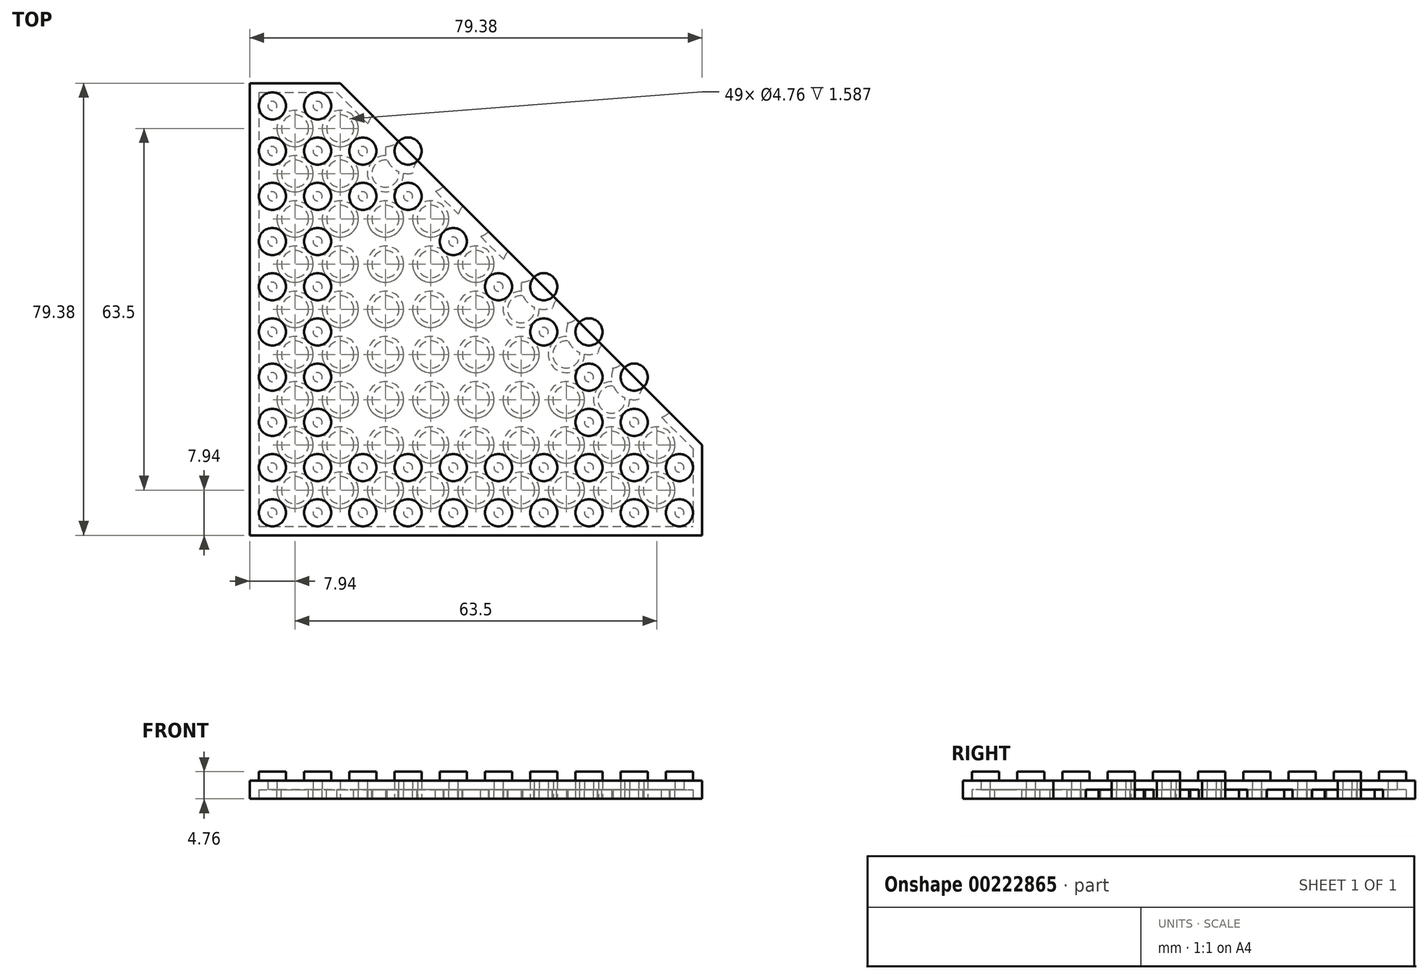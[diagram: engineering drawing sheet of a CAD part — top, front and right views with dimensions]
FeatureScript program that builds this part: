
annotation { "Feature Type Name" : "Feature", "Feature Type Description" : "" }
export const myFeature = defineFeature(function(context is Context, id is Id, definition is map)
    precondition{}
    {
        {
            var Q0;
            Q0=qCreatedBy(makeId("Top.planeOp"),FACE);
            var sketch = newSketch(context, id + "F0", { "sketchPlane" : qUnion([Q0])});
            skLineSegment(sketch, "E0.bottom", {"start": v(-39.69, 39.69) * mm, "end": v(39.69, 39.69) * mm});
            skLineSegment(sketch, "E0.top", {"start": v(-39.69, -39.69) * mm, "end": v(39.69, -39.69) * mm});
            skLineSegment(sketch, "E0.left", {"start": v(-39.69, 39.69) * mm, "end": v(-39.69, -39.69) * mm});
            skLineSegment(sketch, "E0.right", {"start": v(39.69, 39.69) * mm, "end": v(39.69, -39.69) * mm});
            skPoint(sketch, "E0.middle", {"position": v(0, 0) * mm});
            skCircle(sketch, "E1", {"center": v(-35.72, -35.72) * mm, "radius": 2.38 * mm});
            skCircle(sketch, "E2.0.1.0", {"center": v(-35.72, -27.78) * mm, "radius": 2.38 * mm});
            skCircle(sketch, "E2.0.2.0", {"center": v(-35.72, -19.84) * mm, "radius": 2.38 * mm});
            skCircle(sketch, "E2.0.3.0", {"center": v(-35.72, -11.9) * mm, "radius": 2.38 * mm});
            skCircle(sketch, "E2.0.4.0", {"center": v(-35.72, -3.97) * mm, "radius": 2.38 * mm});
            skCircle(sketch, "E2.0.5.0", {"center": v(-35.72, 3.97) * mm, "radius": 2.38 * mm});
            skCircle(sketch, "E2.0.6.0", {"center": v(-35.72, 11.9) * mm, "radius": 2.38 * mm});
            skCircle(sketch, "E2.0.7.0", {"center": v(-35.72, 19.84) * mm, "radius": 2.38 * mm});
            skCircle(sketch, "E2.0.8.0", {"center": v(-35.72, 27.78) * mm, "radius": 2.38 * mm});
            skCircle(sketch, "E2.0.9.0", {"center": v(-35.72, 35.72) * mm, "radius": 2.38 * mm});
            skCircle(sketch, "E2.1.0.0", {"center": v(-27.78, -35.72) * mm, "radius": 2.38 * mm});
            skCircle(sketch, "E2.1.1.0", {"center": v(-27.78, -27.78) * mm, "radius": 2.38 * mm});
            skCircle(sketch, "E2.1.2.0", {"center": v(-27.78, -19.84) * mm, "radius": 2.38 * mm});
            skCircle(sketch, "E2.1.3.0", {"center": v(-27.78, -11.9) * mm, "radius": 2.38 * mm});
            skCircle(sketch, "E2.1.4.0", {"center": v(-27.78, -3.97) * mm, "radius": 2.38 * mm});
            skCircle(sketch, "E2.1.5.0", {"center": v(-27.78, 3.97) * mm, "radius": 2.38 * mm});
            skCircle(sketch, "E2.1.6.0", {"center": v(-27.78, 11.9) * mm, "radius": 2.38 * mm});
            skCircle(sketch, "E2.1.7.0", {"center": v(-27.78, 19.84) * mm, "radius": 2.38 * mm});
            skCircle(sketch, "E2.1.8.0", {"center": v(-27.78, 27.78) * mm, "radius": 2.38 * mm});
            skCircle(sketch, "E2.1.9.0", {"center": v(-27.78, 35.72) * mm, "radius": 2.38 * mm});
            skCircle(sketch, "E2.2.0.0", {"center": v(-19.84, -35.72) * mm, "radius": 2.38 * mm});
            skCircle(sketch, "E2.2.1.0", {"center": v(-19.84, -27.78) * mm, "radius": 2.38 * mm});
            skCircle(sketch, "E2.2.2.0", {"center": v(-19.84, -19.84) * mm, "radius": 2.38 * mm});
            skCircle(sketch, "E2.2.3.0", {"center": v(-19.84, -11.9) * mm, "radius": 2.38 * mm});
            skCircle(sketch, "E2.2.4.0", {"center": v(-19.84, -3.97) * mm, "radius": 2.38 * mm});
            skCircle(sketch, "E2.2.5.0", {"center": v(-19.84, 3.97) * mm, "radius": 2.38 * mm});
            skCircle(sketch, "E2.2.6.0", {"center": v(-19.84, 11.9) * mm, "radius": 2.38 * mm});
            skCircle(sketch, "E2.2.7.0", {"center": v(-19.84, 19.84) * mm, "radius": 2.38 * mm});
            skCircle(sketch, "E2.2.8.0", {"center": v(-19.84, 27.78) * mm, "radius": 2.38 * mm});
            skCircle(sketch, "E2.2.9.0", {"center": v(-19.84, 35.72) * mm, "radius": 2.38 * mm});
            skCircle(sketch, "E2.3.0.0", {"center": v(-11.9, -35.72) * mm, "radius": 2.38 * mm});
            skCircle(sketch, "E2.3.1.0", {"center": v(-11.9, -27.78) * mm, "radius": 2.38 * mm});
            skCircle(sketch, "E2.3.2.0", {"center": v(-11.9, -19.84) * mm, "radius": 2.38 * mm});
            skCircle(sketch, "E2.3.3.0", {"center": v(-11.9, -11.9) * mm, "radius": 2.38 * mm});
            skCircle(sketch, "E2.3.4.0", {"center": v(-11.9, -3.97) * mm, "radius": 2.38 * mm});
            skCircle(sketch, "E2.3.5.0", {"center": v(-11.9, 3.97) * mm, "radius": 2.38 * mm});
            skCircle(sketch, "E2.3.6.0", {"center": v(-11.9, 11.9) * mm, "radius": 2.38 * mm});
            skCircle(sketch, "E2.3.7.0", {"center": v(-11.9, 19.84) * mm, "radius": 2.38 * mm});
            skCircle(sketch, "E2.3.8.0", {"center": v(-11.9, 27.78) * mm, "radius": 2.38 * mm});
            skCircle(sketch, "E2.3.9.0", {"center": v(-11.9, 35.72) * mm, "radius": 2.38 * mm});
            skCircle(sketch, "E2.4.0.0", {"center": v(-3.97, -35.72) * mm, "radius": 2.38 * mm});
            skCircle(sketch, "E2.4.1.0", {"center": v(-3.97, -27.78) * mm, "radius": 2.38 * mm});
            skCircle(sketch, "E2.4.2.0", {"center": v(-3.97, -19.84) * mm, "radius": 2.38 * mm});
            skCircle(sketch, "E2.4.3.0", {"center": v(-3.97, -11.9) * mm, "radius": 2.38 * mm});
            skCircle(sketch, "E2.4.4.0", {"center": v(-3.97, -3.97) * mm, "radius": 2.38 * mm});
            skCircle(sketch, "E2.4.5.0", {"center": v(-3.97, 3.97) * mm, "radius": 2.38 * mm});
            skCircle(sketch, "E2.4.6.0", {"center": v(-3.97, 11.9) * mm, "radius": 2.38 * mm});
            skCircle(sketch, "E2.4.7.0", {"center": v(-3.97, 19.84) * mm, "radius": 2.38 * mm});
            skCircle(sketch, "E2.4.8.0", {"center": v(-3.97, 27.78) * mm, "radius": 2.38 * mm});
            skCircle(sketch, "E2.4.9.0", {"center": v(-3.97, 35.72) * mm, "radius": 2.38 * mm});
            skCircle(sketch, "E2.5.0.0", {"center": v(3.97, -35.72) * mm, "radius": 2.38 * mm});
            skCircle(sketch, "E2.5.1.0", {"center": v(3.97, -27.78) * mm, "radius": 2.38 * mm});
            skCircle(sketch, "E2.5.2.0", {"center": v(3.97, -19.84) * mm, "radius": 2.38 * mm});
            skCircle(sketch, "E2.5.3.0", {"center": v(3.97, -11.9) * mm, "radius": 2.38 * mm});
            skCircle(sketch, "E2.5.4.0", {"center": v(3.97, -3.97) * mm, "radius": 2.38 * mm});
            skCircle(sketch, "E2.5.5.0", {"center": v(3.97, 3.97) * mm, "radius": 2.38 * mm});
            skCircle(sketch, "E2.5.6.0", {"center": v(3.97, 11.9) * mm, "radius": 2.38 * mm});
            skCircle(sketch, "E2.5.7.0", {"center": v(3.97, 19.84) * mm, "radius": 2.38 * mm});
            skCircle(sketch, "E2.5.8.0", {"center": v(3.97, 27.78) * mm, "radius": 2.38 * mm});
            skCircle(sketch, "E2.5.9.0", {"center": v(3.97, 35.72) * mm, "radius": 2.38 * mm});
            skCircle(sketch, "E2.6.0.0", {"center": v(11.9, -35.72) * mm, "radius": 2.38 * mm});
            skCircle(sketch, "E2.6.1.0", {"center": v(11.9, -27.78) * mm, "radius": 2.38 * mm});
            skCircle(sketch, "E2.6.2.0", {"center": v(11.9, -19.84) * mm, "radius": 2.38 * mm});
            skCircle(sketch, "E2.6.3.0", {"center": v(11.9, -11.9) * mm, "radius": 2.38 * mm});
            skCircle(sketch, "E2.6.4.0", {"center": v(11.9, -3.97) * mm, "radius": 2.38 * mm});
            skCircle(sketch, "E2.6.5.0", {"center": v(11.9, 3.97) * mm, "radius": 2.38 * mm});
            skCircle(sketch, "E2.6.6.0", {"center": v(11.9, 11.9) * mm, "radius": 2.38 * mm});
            skCircle(sketch, "E2.6.7.0", {"center": v(11.9, 19.84) * mm, "radius": 2.38 * mm});
            skCircle(sketch, "E2.6.8.0", {"center": v(11.9, 27.78) * mm, "radius": 2.38 * mm});
            skCircle(sketch, "E2.6.9.0", {"center": v(11.9, 35.72) * mm, "radius": 2.38 * mm});
            skCircle(sketch, "E2.7.0.0", {"center": v(19.84, -35.72) * mm, "radius": 2.38 * mm});
            skCircle(sketch, "E2.7.1.0", {"center": v(19.84, -27.78) * mm, "radius": 2.38 * mm});
            skCircle(sketch, "E2.7.2.0", {"center": v(19.84, -19.84) * mm, "radius": 2.38 * mm});
            skCircle(sketch, "E2.7.3.0", {"center": v(19.84, -11.9) * mm, "radius": 2.38 * mm});
            skCircle(sketch, "E2.7.4.0", {"center": v(19.84, -3.97) * mm, "radius": 2.38 * mm});
            skCircle(sketch, "E2.7.5.0", {"center": v(19.84, 3.97) * mm, "radius": 2.38 * mm});
            skCircle(sketch, "E2.7.6.0", {"center": v(19.84, 11.9) * mm, "radius": 2.38 * mm});
            skCircle(sketch, "E2.7.7.0", {"center": v(19.84, 19.84) * mm, "radius": 2.38 * mm});
            skCircle(sketch, "E2.7.8.0", {"center": v(19.84, 27.78) * mm, "radius": 2.38 * mm});
            skCircle(sketch, "E2.7.9.0", {"center": v(19.84, 35.72) * mm, "radius": 2.38 * mm});
            skCircle(sketch, "E2.8.0.0", {"center": v(27.78, -35.72) * mm, "radius": 2.38 * mm});
            skCircle(sketch, "E2.8.1.0", {"center": v(27.78, -27.78) * mm, "radius": 2.38 * mm});
            skCircle(sketch, "E2.8.2.0", {"center": v(27.78, -19.84) * mm, "radius": 2.38 * mm});
            skCircle(sketch, "E2.8.3.0", {"center": v(27.78, -11.9) * mm, "radius": 2.38 * mm});
            skCircle(sketch, "E2.8.4.0", {"center": v(27.78, -3.97) * mm, "radius": 2.38 * mm});
            skCircle(sketch, "E2.8.5.0", {"center": v(27.78, 3.97) * mm, "radius": 2.38 * mm});
            skCircle(sketch, "E2.8.6.0", {"center": v(27.78, 11.9) * mm, "radius": 2.38 * mm});
            skCircle(sketch, "E2.8.7.0", {"center": v(27.78, 19.84) * mm, "radius": 2.38 * mm});
            skCircle(sketch, "E2.8.8.0", {"center": v(27.78, 27.78) * mm, "radius": 2.38 * mm});
            skCircle(sketch, "E2.8.9.0", {"center": v(27.78, 35.72) * mm, "radius": 2.38 * mm});
            skCircle(sketch, "E2.9.0.0", {"center": v(35.72, -35.72) * mm, "radius": 2.38 * mm});
            skCircle(sketch, "E2.9.1.0", {"center": v(35.72, -27.78) * mm, "radius": 2.38 * mm});
            skCircle(sketch, "E2.9.2.0", {"center": v(35.72, -19.84) * mm, "radius": 2.38 * mm});
            skCircle(sketch, "E2.9.3.0", {"center": v(35.72, -11.9) * mm, "radius": 2.38 * mm});
            skCircle(sketch, "E2.9.4.0", {"center": v(35.72, -3.97) * mm, "radius": 2.38 * mm});
            skCircle(sketch, "E2.9.5.0", {"center": v(35.72, 3.97) * mm, "radius": 2.38 * mm});
            skCircle(sketch, "E2.9.6.0", {"center": v(35.72, 11.9) * mm, "radius": 2.38 * mm});
            skCircle(sketch, "E2.9.7.0", {"center": v(35.72, 19.84) * mm, "radius": 2.38 * mm});
            skCircle(sketch, "E2.9.8.0", {"center": v(35.72, 27.78) * mm, "radius": 2.38 * mm});
            skCircle(sketch, "E2.9.9.0", {"center": v(35.72, 35.72) * mm, "radius": 2.38 * mm});
            skLineSegment(sketch, "E2.direction1", {"start": v(-35.72, -35.72) * mm, "end": v(-27.78, -35.72) * mm, "construction": true});
            skLineSegment(sketch, "E2.direction2", {"start": v(-35.72, -35.72) * mm, "end": v(-35.72, -27.78) * mm, "construction": true});
            skPoint(sketch, "E3", {"position": v(-23.81, 39.69) * mm});
            skPoint(sketch, "E4", {"position": v(39.69, -23.81) * mm});
            skLineSegment(sketch, "E5", {"start": v(-23.81, 39.69) * mm, "end": v(39.69, -23.81) * mm});
            skSolve(sketch);
        }
        {
            var Q0;
            {var subQ9=sQuery(id+"F0.wireOp",EDGE,"E0.top");Q0=makeQuery(id+"F0.imprint","IMPRINT",FACE,{"disambiguationData":[TD([[makeQuery(id+"F0.imprint","IMPRINT",EDGE,{"derivedFrom":subQ9}),1.0]])]});}
            var Q1;
            {var subQ0=sQuery(id+"F0.wireOp",EDGE,"E5");var subQ1=sQuery(id+"F0.wireOp",EDGE,"E2.2.9.0");var subQ2=makeQuery(id+"F0.imprint","INTERSECT",VERTEX,{"disambiguationData":[OD(0.0)],"derivedFrom":[subQ1,subQ0]});Q1=makeQuery(id+"F0.imprint","IMPRINT",FACE,{"disambiguationData":[TD([[makeQuery(id+"F0.imprint","IMPRINT",EDGE,{"disambiguationData":[TD([[subQ2,-1.0]])],"derivedFrom":subQ1}),1.0]])]});}
            var Q2;
            {var subQ0=sQuery(id+"F0.wireOp",EDGE,"E5");var subQ1=sQuery(id+"F0.wireOp",EDGE,"E2.3.8.0");var subQ2=makeQuery(id+"F0.imprint","INTERSECT",VERTEX,{"disambiguationData":[OD(0.0)],"derivedFrom":[subQ1,subQ0]});Q2=makeQuery(id+"F0.imprint","IMPRINT",FACE,{"disambiguationData":[TD([[makeQuery(id+"F0.imprint","IMPRINT",EDGE,{"disambiguationData":[TD([[subQ2,-1.0]])],"derivedFrom":subQ1}),1.0]])]});}
            var Q3;
            {var subQ0=sQuery(id+"F0.wireOp",EDGE,"E5");var subQ1=sQuery(id+"F0.wireOp",EDGE,"E2.4.7.0");var subQ2=makeQuery(id+"F0.imprint","INTERSECT",VERTEX,{"disambiguationData":[OD(0.0)],"derivedFrom":[subQ1,subQ0]});Q3=makeQuery(id+"F0.imprint","IMPRINT",FACE,{"disambiguationData":[TD([[makeQuery(id+"F0.imprint","IMPRINT",EDGE,{"disambiguationData":[TD([[subQ2,-1.0]])],"derivedFrom":subQ1}),1.0]])]});}
            var Q4;
            {var subQ0=sQuery(id+"F0.wireOp",EDGE,"E5");var subQ1=sQuery(id+"F0.wireOp",EDGE,"E2.5.6.0");var subQ2=makeQuery(id+"F0.imprint","INTERSECT",VERTEX,{"disambiguationData":[OD(0.0)],"derivedFrom":[subQ1,subQ0]});Q4=makeQuery(id+"F0.imprint","IMPRINT",FACE,{"disambiguationData":[TD([[makeQuery(id+"F0.imprint","IMPRINT",EDGE,{"disambiguationData":[TD([[subQ2,-1.0]])],"derivedFrom":subQ1}),1.0]])]});}
            var Q5;
            {var subQ0=sQuery(id+"F0.wireOp",EDGE,"E5");var subQ1=sQuery(id+"F0.wireOp",EDGE,"E2.6.5.0");var subQ2=makeQuery(id+"F0.imprint","INTERSECT",VERTEX,{"disambiguationData":[OD(0.0)],"derivedFrom":[subQ1,subQ0]});Q5=makeQuery(id+"F0.imprint","IMPRINT",FACE,{"disambiguationData":[TD([[makeQuery(id+"F0.imprint","IMPRINT",EDGE,{"disambiguationData":[TD([[subQ2,-1.0]])],"derivedFrom":subQ1}),1.0]])]});}
            var Q6;
            {var subQ0=sQuery(id+"F0.wireOp",EDGE,"E5");var subQ1=sQuery(id+"F0.wireOp",EDGE,"E2.7.4.0");var subQ2=makeQuery(id+"F0.imprint","INTERSECT",VERTEX,{"disambiguationData":[OD(0.0)],"derivedFrom":[subQ1,subQ0]});Q6=makeQuery(id+"F0.imprint","IMPRINT",FACE,{"disambiguationData":[TD([[makeQuery(id+"F0.imprint","IMPRINT",EDGE,{"disambiguationData":[TD([[subQ2,-1.0]])],"derivedFrom":subQ1}),1.0]])]});}
            var Q7;
            {var subQ0=sQuery(id+"F0.wireOp",EDGE,"E5");var subQ1=sQuery(id+"F0.wireOp",EDGE,"E2.8.3.0");var subQ2=makeQuery(id+"F0.imprint","INTERSECT",VERTEX,{"disambiguationData":[OD(0.0)],"derivedFrom":[subQ1,subQ0]});Q7=makeQuery(id+"F0.imprint","IMPRINT",FACE,{"disambiguationData":[TD([[makeQuery(id+"F0.imprint","IMPRINT",EDGE,{"disambiguationData":[TD([[subQ2,-1.0]])],"derivedFrom":subQ1}),1.0]])]});}
            var Q8;
            {var subQ0=sQuery(id+"F0.wireOp",EDGE,"E5");var subQ1=sQuery(id+"F0.wireOp",EDGE,"E2.9.2.0");var subQ2=makeQuery(id+"F0.imprint","INTERSECT",VERTEX,{"disambiguationData":[OD(0.0)],"derivedFrom":[subQ1,subQ0]});Q8=makeQuery(id+"F0.imprint","IMPRINT",FACE,{"disambiguationData":[TD([[makeQuery(id+"F0.imprint","IMPRINT",EDGE,{"disambiguationData":[TD([[subQ2,-1.0]])],"derivedFrom":subQ1}),1.0]])]});}
            var Q9;
            Q9=makeQuery(id+"F0.imprint","IMPRINT",FACE,{"disambiguationData":[TD([[makeQuery(id+"F0.imprint","IMPRINT",EDGE,{"derivedFrom":sQuery(id+"F0.wireOp",EDGE,"E2.2.6.0")}),1.0]])]});
            var Q10;
            Q10=makeQuery(id+"F0.imprint","IMPRINT",FACE,{"disambiguationData":[TD([[makeQuery(id+"F0.imprint","IMPRINT",EDGE,{"derivedFrom":sQuery(id+"F0.wireOp",EDGE,"E2.3.6.0")}),1.0]])]});
            var Q11;
            Q11=makeQuery(id+"F0.imprint","IMPRINT",FACE,{"disambiguationData":[TD([[makeQuery(id+"F0.imprint","IMPRINT",EDGE,{"derivedFrom":sQuery(id+"F0.wireOp",EDGE,"E2.2.5.0")}),1.0]])]});
            var Q12;
            Q12=makeQuery(id+"F0.imprint","IMPRINT",FACE,{"disambiguationData":[TD([[makeQuery(id+"F0.imprint","IMPRINT",EDGE,{"derivedFrom":sQuery(id+"F0.wireOp",EDGE,"E2.3.5.0")}),1.0]])]});
            var Q13;
            Q13=makeQuery(id+"F0.imprint","IMPRINT",FACE,{"disambiguationData":[TD([[makeQuery(id+"F0.imprint","IMPRINT",EDGE,{"derivedFrom":sQuery(id+"F0.wireOp",EDGE,"E2.2.4.0")}),1.0]])]});
            var Q14;
            Q14=makeQuery(id+"F0.imprint","IMPRINT",FACE,{"disambiguationData":[TD([[makeQuery(id+"F0.imprint","IMPRINT",EDGE,{"derivedFrom":sQuery(id+"F0.wireOp",EDGE,"E2.2.3.0")}),1.0]])]});
            var Q15;
            Q15=makeQuery(id+"F0.imprint","IMPRINT",FACE,{"disambiguationData":[TD([[makeQuery(id+"F0.imprint","IMPRINT",EDGE,{"derivedFrom":sQuery(id+"F0.wireOp",EDGE,"E2.2.2.0")}),1.0]])]});
            var Q16;
            Q16=makeQuery(id+"F0.imprint","IMPRINT",FACE,{"disambiguationData":[TD([[makeQuery(id+"F0.imprint","IMPRINT",EDGE,{"derivedFrom":sQuery(id+"F0.wireOp",EDGE,"E2.3.2.0")}),1.0]])]});
            var Q17;
            Q17=makeQuery(id+"F0.imprint","IMPRINT",FACE,{"disambiguationData":[TD([[makeQuery(id+"F0.imprint","IMPRINT",EDGE,{"derivedFrom":sQuery(id+"F0.wireOp",EDGE,"E2.4.2.0")}),1.0]])]});
            var Q18;
            Q18=makeQuery(id+"F0.imprint","IMPRINT",FACE,{"disambiguationData":[TD([[makeQuery(id+"F0.imprint","IMPRINT",EDGE,{"derivedFrom":sQuery(id+"F0.wireOp",EDGE,"E2.6.2.0")}),1.0]])]});
            var Q19;
            Q19=makeQuery(id+"F0.imprint","IMPRINT",FACE,{"disambiguationData":[TD([[makeQuery(id+"F0.imprint","IMPRINT",EDGE,{"derivedFrom":sQuery(id+"F0.wireOp",EDGE,"E2.6.3.0")}),1.0]])]});
            var Q20;
            Q20=makeQuery(id+"F0.imprint","IMPRINT",FACE,{"disambiguationData":[TD([[makeQuery(id+"F0.imprint","IMPRINT",EDGE,{"derivedFrom":sQuery(id+"F0.wireOp",EDGE,"E2.5.4.0")}),1.0]])]});
            var Q21;
            Q21=makeQuery(id+"F0.imprint","IMPRINT",FACE,{"disambiguationData":[TD([[makeQuery(id+"F0.imprint","IMPRINT",EDGE,{"derivedFrom":sQuery(id+"F0.wireOp",EDGE,"E2.4.5.0")}),1.0]])]});
            var Q22;
            Q22=makeQuery(id+"F0.imprint","IMPRINT",FACE,{"disambiguationData":[TD([[makeQuery(id+"F0.imprint","IMPRINT",EDGE,{"derivedFrom":sQuery(id+"F0.wireOp",EDGE,"E2.5.2.0")}),1.0]])]});
            var Q23;
            Q23=makeQuery(id+"F0.imprint","IMPRINT",FACE,{"disambiguationData":[TD([[makeQuery(id+"F0.imprint","IMPRINT",EDGE,{"derivedFrom":sQuery(id+"F0.wireOp",EDGE,"E2.5.3.0")}),1.0]])]});
            var Q24;
            Q24=makeQuery(id+"F0.imprint","IMPRINT",FACE,{"disambiguationData":[TD([[makeQuery(id+"F0.imprint","IMPRINT",EDGE,{"derivedFrom":sQuery(id+"F0.wireOp",EDGE,"E2.4.3.0")}),1.0]])]});
            var Q25;
            Q25=makeQuery(id+"F0.imprint","IMPRINT",FACE,{"disambiguationData":[TD([[makeQuery(id+"F0.imprint","IMPRINT",EDGE,{"derivedFrom":sQuery(id+"F0.wireOp",EDGE,"E2.3.3.0")}),1.0]])]});
            var Q26;
            Q26=makeQuery(id+"F0.imprint","IMPRINT",FACE,{"disambiguationData":[TD([[makeQuery(id+"F0.imprint","IMPRINT",EDGE,{"derivedFrom":sQuery(id+"F0.wireOp",EDGE,"E2.3.4.0")}),1.0]])]});
            var Q27;
            Q27=makeQuery(id+"F0.imprint","IMPRINT",FACE,{"disambiguationData":[TD([[makeQuery(id+"F0.imprint","IMPRINT",EDGE,{"derivedFrom":sQuery(id+"F0.wireOp",EDGE,"E2.4.4.0")}),1.0]])]});
            extrude(context, id + "F1", {"entities" : qUnion([Q0, Q1, Q2, Q3, Q4, Q5, Q6, Q7, Q8, Q9, Q10, Q11, Q12, Q13, Q14, Q15, Q16, Q17, Q18, Q19, Q20, Q21, Q22, Q23, Q24, Q25, Q26, Q27]), "depth" : 3.17 * mm});
        }
        {
            var Q0;
            Q0=makeQuery(id+"F0.imprint","IMPRINT",FACE,{"disambiguationData":[TD([[makeQuery(id+"F0.imprint","IMPRINT",EDGE,{"derivedFrom":sQuery(id+"F0.wireOp",EDGE,"E2.0.9.0")}),1.0]])]});
            var Q1;
            Q1=makeQuery(id+"F0.imprint","IMPRINT",FACE,{"disambiguationData":[TD([[makeQuery(id+"F0.imprint","IMPRINT",EDGE,{"derivedFrom":sQuery(id+"F0.wireOp",EDGE,"E2.1.9.0")}),1.0]])]});
            var Q2;
            Q2=makeQuery(id+"F0.imprint","IMPRINT",FACE,{"disambiguationData":[TD([[makeQuery(id+"F0.imprint","IMPRINT",EDGE,{"derivedFrom":sQuery(id+"F0.wireOp",EDGE,"E2.0.8.0")}),1.0]])]});
            var Q3;
            Q3=makeQuery(id+"F0.imprint","IMPRINT",FACE,{"disambiguationData":[TD([[makeQuery(id+"F0.imprint","IMPRINT",EDGE,{"derivedFrom":sQuery(id+"F0.wireOp",EDGE,"E2.1.8.0")}),1.0]])]});
            var Q4;
            Q4=makeQuery(id+"F0.imprint","IMPRINT",FACE,{"disambiguationData":[TD([[makeQuery(id+"F0.imprint","IMPRINT",EDGE,{"derivedFrom":sQuery(id+"F0.wireOp",EDGE,"E2.0.7.0")}),1.0]])]});
            var Q5;
            Q5=makeQuery(id+"F0.imprint","IMPRINT",FACE,{"disambiguationData":[TD([[makeQuery(id+"F0.imprint","IMPRINT",EDGE,{"derivedFrom":sQuery(id+"F0.wireOp",EDGE,"E2.0.6.0")}),1.0]])]});
            var Q6;
            Q6=makeQuery(id+"F0.imprint","IMPRINT",FACE,{"disambiguationData":[TD([[makeQuery(id+"F0.imprint","IMPRINT",EDGE,{"derivedFrom":sQuery(id+"F0.wireOp",EDGE,"E2.1.6.0")}),1.0]])]});
            var Q7;
            Q7=makeQuery(id+"F0.imprint","IMPRINT",FACE,{"disambiguationData":[TD([[makeQuery(id+"F0.imprint","IMPRINT",EDGE,{"derivedFrom":sQuery(id+"F0.wireOp",EDGE,"E2.1.7.0")}),1.0]])]});
            var Q8;
            Q8=makeQuery(id+"F0.imprint","IMPRINT",FACE,{"disambiguationData":[TD([[makeQuery(id+"F0.imprint","IMPRINT",EDGE,{"derivedFrom":sQuery(id+"F0.wireOp",EDGE,"E2.0.5.0")}),1.0]])]});
            var Q9;
            Q9=makeQuery(id+"F0.imprint","IMPRINT",FACE,{"disambiguationData":[TD([[makeQuery(id+"F0.imprint","IMPRINT",EDGE,{"derivedFrom":sQuery(id+"F0.wireOp",EDGE,"E2.1.5.0")}),1.0]])]});
            var Q10;
            Q10=makeQuery(id+"F0.imprint","IMPRINT",FACE,{"disambiguationData":[TD([[makeQuery(id+"F0.imprint","IMPRINT",EDGE,{"derivedFrom":sQuery(id+"F0.wireOp",EDGE,"E2.1.4.0")}),1.0]])]});
            var Q11;
            Q11=makeQuery(id+"F0.imprint","IMPRINT",FACE,{"disambiguationData":[TD([[makeQuery(id+"F0.imprint","IMPRINT",EDGE,{"derivedFrom":sQuery(id+"F0.wireOp",EDGE,"E2.0.4.0")}),1.0]])]});
            var Q12;
            Q12=makeQuery(id+"F0.imprint","IMPRINT",FACE,{"disambiguationData":[TD([[makeQuery(id+"F0.imprint","IMPRINT",EDGE,{"derivedFrom":sQuery(id+"F0.wireOp",EDGE,"E2.0.3.0")}),1.0]])]});
            var Q13;
            Q13=makeQuery(id+"F0.imprint","IMPRINT",FACE,{"disambiguationData":[TD([[makeQuery(id+"F0.imprint","IMPRINT",EDGE,{"derivedFrom":sQuery(id+"F0.wireOp",EDGE,"E2.1.3.0")}),1.0]])]});
            var Q14;
            Q14=makeQuery(id+"F0.imprint","IMPRINT",FACE,{"disambiguationData":[TD([[makeQuery(id+"F0.imprint","IMPRINT",EDGE,{"derivedFrom":sQuery(id+"F0.wireOp",EDGE,"E2.1.2.0")}),1.0]])]});
            var Q15;
            Q15=makeQuery(id+"F0.imprint","IMPRINT",FACE,{"disambiguationData":[TD([[makeQuery(id+"F0.imprint","IMPRINT",EDGE,{"derivedFrom":sQuery(id+"F0.wireOp",EDGE,"E2.0.2.0")}),1.0]])]});
            var Q16;
            Q16=makeQuery(id+"F0.imprint","IMPRINT",FACE,{"disambiguationData":[TD([[makeQuery(id+"F0.imprint","IMPRINT",EDGE,{"derivedFrom":sQuery(id+"F0.wireOp",EDGE,"E2.0.1.0")}),1.0]])]});
            var Q17;
            Q17=makeQuery(id+"F0.imprint","IMPRINT",FACE,{"disambiguationData":[TD([[makeQuery(id+"F0.imprint","IMPRINT",EDGE,{"derivedFrom":sQuery(id+"F0.wireOp",EDGE,"E2.1.1.0")}),1.0]])]});
            var Q18;
            Q18=makeQuery(id+"F0.imprint","IMPRINT",FACE,{"disambiguationData":[TD([[makeQuery(id+"F0.imprint","IMPRINT",EDGE,{"derivedFrom":sQuery(id+"F0.wireOp",EDGE,"E2.1.0.0")}),1.0]])]});
            var Q19;
            Q19=makeQuery(id+"F0.imprint","IMPRINT",FACE,{"disambiguationData":[TD([[makeQuery(id+"F0.imprint","IMPRINT",EDGE,{"derivedFrom":sQuery(id+"F0.wireOp",EDGE,"E1")}),1.0]])]});
            var Q20;
            Q20=makeQuery(id+"F0.imprint","IMPRINT",FACE,{"disambiguationData":[TD([[makeQuery(id+"F0.imprint","IMPRINT",EDGE,{"derivedFrom":sQuery(id+"F0.wireOp",EDGE,"E2.2.0.0")}),1.0]])]});
            var Q21;
            Q21=makeQuery(id+"F0.imprint","IMPRINT",FACE,{"disambiguationData":[TD([[makeQuery(id+"F0.imprint","IMPRINT",EDGE,{"derivedFrom":sQuery(id+"F0.wireOp",EDGE,"E2.2.1.0")}),1.0]])]});
            var Q22;
            Q22=makeQuery(id+"F0.imprint","IMPRINT",FACE,{"disambiguationData":[TD([[makeQuery(id+"F0.imprint","IMPRINT",EDGE,{"derivedFrom":sQuery(id+"F0.wireOp",EDGE,"E2.3.0.0")}),1.0]])]});
            var Q23;
            Q23=makeQuery(id+"F0.imprint","IMPRINT",FACE,{"disambiguationData":[TD([[makeQuery(id+"F0.imprint","IMPRINT",EDGE,{"derivedFrom":sQuery(id+"F0.wireOp",EDGE,"E2.3.1.0")}),1.0]])]});
            var Q24;
            Q24=makeQuery(id+"F0.imprint","IMPRINT",FACE,{"disambiguationData":[TD([[makeQuery(id+"F0.imprint","IMPRINT",EDGE,{"derivedFrom":sQuery(id+"F0.wireOp",EDGE,"E2.4.1.0")}),1.0]])]});
            var Q25;
            Q25=makeQuery(id+"F0.imprint","IMPRINT",FACE,{"disambiguationData":[TD([[makeQuery(id+"F0.imprint","IMPRINT",EDGE,{"derivedFrom":sQuery(id+"F0.wireOp",EDGE,"E2.4.0.0")}),1.0]])]});
            var Q26;
            Q26=makeQuery(id+"F0.imprint","IMPRINT",FACE,{"disambiguationData":[TD([[makeQuery(id+"F0.imprint","IMPRINT",EDGE,{"derivedFrom":sQuery(id+"F0.wireOp",EDGE,"E2.5.0.0")}),1.0]])]});
            var Q27;
            Q27=makeQuery(id+"F0.imprint","IMPRINT",FACE,{"disambiguationData":[TD([[makeQuery(id+"F0.imprint","IMPRINT",EDGE,{"derivedFrom":sQuery(id+"F0.wireOp",EDGE,"E2.5.1.0")}),1.0]])]});
            var Q28;
            Q28=makeQuery(id+"F0.imprint","IMPRINT",FACE,{"disambiguationData":[TD([[makeQuery(id+"F0.imprint","IMPRINT",EDGE,{"derivedFrom":sQuery(id+"F0.wireOp",EDGE,"E2.6.0.0")}),1.0]])]});
            var Q29;
            Q29=makeQuery(id+"F0.imprint","IMPRINT",FACE,{"disambiguationData":[TD([[makeQuery(id+"F0.imprint","IMPRINT",EDGE,{"derivedFrom":sQuery(id+"F0.wireOp",EDGE,"E2.6.1.0")}),1.0]])]});
            var Q30;
            Q30=makeQuery(id+"F0.imprint","IMPRINT",FACE,{"disambiguationData":[TD([[makeQuery(id+"F0.imprint","IMPRINT",EDGE,{"derivedFrom":sQuery(id+"F0.wireOp",EDGE,"E2.7.1.0")}),1.0]])]});
            var Q31;
            Q31=makeQuery(id+"F0.imprint","IMPRINT",FACE,{"disambiguationData":[TD([[makeQuery(id+"F0.imprint","IMPRINT",EDGE,{"derivedFrom":sQuery(id+"F0.wireOp",EDGE,"E2.7.0.0")}),1.0]])]});
            var Q32;
            Q32=makeQuery(id+"F0.imprint","IMPRINT",FACE,{"disambiguationData":[TD([[makeQuery(id+"F0.imprint","IMPRINT",EDGE,{"derivedFrom":sQuery(id+"F0.wireOp",EDGE,"E2.8.0.0")}),1.0]])]});
            var Q33;
            Q33=makeQuery(id+"F0.imprint","IMPRINT",FACE,{"disambiguationData":[TD([[makeQuery(id+"F0.imprint","IMPRINT",EDGE,{"derivedFrom":sQuery(id+"F0.wireOp",EDGE,"E2.8.1.0")}),1.0]])]});
            var Q34;
            Q34=makeQuery(id+"F0.imprint","IMPRINT",FACE,{"disambiguationData":[TD([[makeQuery(id+"F0.imprint","IMPRINT",EDGE,{"derivedFrom":sQuery(id+"F0.wireOp",EDGE,"E2.9.1.0")}),1.0]])]});
            var Q35;
            Q35=makeQuery(id+"F0.imprint","IMPRINT",FACE,{"disambiguationData":[TD([[makeQuery(id+"F0.imprint","IMPRINT",EDGE,{"derivedFrom":sQuery(id+"F0.wireOp",EDGE,"E2.9.0.0")}),1.0]])]});
            var Q36;
            Q36=makeQuery(id+"F0.imprint","IMPRINT",FACE,{"disambiguationData":[TD([[makeQuery(id+"F0.imprint","IMPRINT",EDGE,{"derivedFrom":sQuery(id+"F0.wireOp",EDGE,"E2.2.8.0")}),1.0]])]});
            var Q37;
            Q37=makeQuery(id+"F0.imprint","IMPRINT",FACE,{"disambiguationData":[TD([[makeQuery(id+"F0.imprint","IMPRINT",EDGE,{"derivedFrom":sQuery(id+"F0.wireOp",EDGE,"E2.3.7.0")}),1.0]])]});
            var Q38;
            Q38=makeQuery(id+"F0.imprint","IMPRINT",FACE,{"disambiguationData":[TD([[makeQuery(id+"F0.imprint","IMPRINT",EDGE,{"derivedFrom":sQuery(id+"F0.wireOp",EDGE,"E2.4.6.0")}),1.0]])]});
            var Q39;
            Q39=makeQuery(id+"F0.imprint","IMPRINT",FACE,{"disambiguationData":[TD([[makeQuery(id+"F0.imprint","IMPRINT",EDGE,{"derivedFrom":sQuery(id+"F0.wireOp",EDGE,"E2.5.5.0")}),1.0]])]});
            var Q40;
            Q40=makeQuery(id+"F0.imprint","IMPRINT",FACE,{"disambiguationData":[TD([[makeQuery(id+"F0.imprint","IMPRINT",EDGE,{"derivedFrom":sQuery(id+"F0.wireOp",EDGE,"E2.6.4.0")}),1.0]])]});
            var Q41;
            Q41=makeQuery(id+"F0.imprint","IMPRINT",FACE,{"disambiguationData":[TD([[makeQuery(id+"F0.imprint","IMPRINT",EDGE,{"derivedFrom":sQuery(id+"F0.wireOp",EDGE,"E2.7.3.0")}),1.0]])]});
            var Q42;
            Q42=makeQuery(id+"F0.imprint","IMPRINT",FACE,{"disambiguationData":[TD([[makeQuery(id+"F0.imprint","IMPRINT",EDGE,{"derivedFrom":sQuery(id+"F0.wireOp",EDGE,"E2.8.2.0")}),1.0]])]});
            var Q43;
            Q43=makeQuery(id+"F0.imprint","IMPRINT",FACE,{"disambiguationData":[TD([[makeQuery(id+"F0.imprint","IMPRINT",EDGE,{"derivedFrom":sQuery(id+"F0.wireOp",EDGE,"E2.7.2.0")}),1.0]])]});
            var Q44;
            Q44=makeQuery(id+"F0.imprint","IMPRINT",FACE,{"disambiguationData":[TD([[makeQuery(id+"F0.imprint","IMPRINT",EDGE,{"derivedFrom":sQuery(id+"F0.wireOp",EDGE,"E2.2.7.0")}),1.0]])]});
            extrude(context, id + "F2", {"entities" : qUnion([Q0, Q1, Q2, Q3, Q4, Q5, Q6, Q7, Q8, Q9, Q10, Q11, Q12, Q13, Q14, Q15, Q16, Q17, Q18, Q19, Q20, Q21, Q22, Q23, Q24, Q25, Q26, Q27, Q28, Q29, Q30, Q31, Q32, Q33, Q34, Q35, Q36, Q37, Q38, Q39, Q40, Q41, Q42, Q43, Q44]), "operationType" : NewBodyOperationType.ADD, "depth" : 4.76 * mm});
        }
        {
            var Q0;
            {var subQ0=sQuery(id+"F0.wireOp",EDGE,"E2.9.1.0");var subQ1=sQuery(id+"F0.wireOp",EDGE,"E2.9.0.0");var subQ2=sQuery(id+"F0.wireOp",EDGE,"E2.8.2.0");var subQ3=sQuery(id+"F0.wireOp",EDGE,"E2.8.1.0");var subQ4=sQuery(id+"F0.wireOp",EDGE,"E2.8.0.0");var subQ5=sQuery(id+"F0.wireOp",EDGE,"E2.7.3.0");var subQ6=sQuery(id+"F0.wireOp",EDGE,"E2.7.2.0");var subQ7=sQuery(id+"F0.wireOp",EDGE,"E2.7.1.0");var subQ8=sQuery(id+"F0.wireOp",EDGE,"E2.7.0.0");var subQ9=sQuery(id+"F0.wireOp",EDGE,"E2.6.4.0");var subQ10=sQuery(id+"F0.wireOp",EDGE,"E2.6.1.0");var subQ11=sQuery(id+"F0.wireOp",EDGE,"E2.6.0.0");var subQ12=sQuery(id+"F0.wireOp",EDGE,"E2.5.5.0");var subQ13=sQuery(id+"F0.wireOp",EDGE,"E2.5.1.0");var subQ14=sQuery(id+"F0.wireOp",EDGE,"E2.5.0.0");var subQ15=sQuery(id+"F0.wireOp",EDGE,"E2.4.6.0");var subQ16=sQuery(id+"F0.wireOp",EDGE,"E2.4.1.0");var subQ17=sQuery(id+"F0.wireOp",EDGE,"E2.4.0.0");var subQ18=sQuery(id+"F0.wireOp",EDGE,"E2.3.7.0");var subQ19=sQuery(id+"F0.wireOp",EDGE,"E2.3.1.0");var subQ20=sQuery(id+"F0.wireOp",EDGE,"E2.3.0.0");var subQ21=sQuery(id+"F0.wireOp",EDGE,"E2.2.8.0");var subQ22=sQuery(id+"F0.wireOp",EDGE,"E2.2.7.0");var subQ23=sQuery(id+"F0.wireOp",EDGE,"E2.2.1.0");var subQ24=sQuery(id+"F0.wireOp",EDGE,"E2.2.0.0");var subQ25=sQuery(id+"F0.wireOp",EDGE,"E2.1.9.0");var subQ26=sQuery(id+"F0.wireOp",EDGE,"E2.1.8.0");var subQ27=sQuery(id+"F0.wireOp",EDGE,"E2.1.7.0");var subQ28=sQuery(id+"F0.wireOp",EDGE,"E2.1.6.0");var subQ29=sQuery(id+"F0.wireOp",EDGE,"E2.1.5.0");var subQ30=sQuery(id+"F0.wireOp",EDGE,"E2.1.4.0");var subQ31=sQuery(id+"F0.wireOp",EDGE,"E2.1.3.0");var subQ32=sQuery(id+"F0.wireOp",EDGE,"E2.1.2.0");var subQ33=sQuery(id+"F0.wireOp",EDGE,"E2.1.1.0");var subQ34=sQuery(id+"F0.wireOp",EDGE,"E2.1.0.0");var subQ35=sQuery(id+"F0.wireOp",EDGE,"E2.0.9.0");var subQ36=sQuery(id+"F0.wireOp",EDGE,"E2.0.8.0");var subQ37=sQuery(id+"F0.wireOp",EDGE,"E2.0.7.0");var subQ38=sQuery(id+"F0.wireOp",EDGE,"E2.0.6.0");var subQ39=sQuery(id+"F0.wireOp",EDGE,"E2.0.5.0");var subQ40=sQuery(id+"F0.wireOp",EDGE,"E2.0.4.0");var subQ41=sQuery(id+"F0.wireOp",EDGE,"E2.0.3.0");var subQ42=sQuery(id+"F0.wireOp",EDGE,"E2.0.2.0");var subQ43=sQuery(id+"F0.wireOp",EDGE,"E2.0.1.0");var subQ44=sQuery(id+"F0.wireOp",EDGE,"E1");Q0=makeQuery(id+"F2.boolean.opBoolean","MERGE",FACE,{"derivedFrom":[makeQuery(id+"F1.opExtrude","CAP_FACE",FACE,{"disambiguationData":[OSD([sQuery(id+"F0.wireOp",EDGE,"E0.bottom"),sQuery(id+"F0.wireOp",EDGE,"E0.top"),sQuery(id+"F0.wireOp",EDGE,"E0.left"),sQuery(id+"F0.wireOp",EDGE,"E0.right"),subQ44,subQ43,subQ42,subQ41,subQ40,subQ39,subQ38,subQ37,subQ36,subQ35,subQ34,subQ33,subQ32,subQ31,subQ30,subQ29,subQ28,subQ27,subQ26,subQ25,subQ24,subQ23,subQ22,subQ21,subQ20,subQ19,subQ18,subQ17,subQ16,subQ15,subQ14,subQ13,subQ12,subQ11,subQ10,subQ9,subQ8,subQ7,subQ6,subQ5,subQ4,subQ3,subQ2,subQ1,subQ0,sQuery(id+"F0.wireOp",EDGE,"E5")])],"isStart":true}),makeQuery(id+"F2.opExtrude","CAP_FACE",FACE,{"disambiguationData":[OSD([subQ44])],"isStart":true}),makeQuery(id+"F2.opExtrude","CAP_FACE",FACE,{"disambiguationData":[OSD([subQ43])],"isStart":true}),makeQuery(id+"F2.opExtrude","CAP_FACE",FACE,{"disambiguationData":[OSD([subQ42])],"isStart":true}),makeQuery(id+"F2.opExtrude","CAP_FACE",FACE,{"disambiguationData":[OSD([subQ41])],"isStart":true}),makeQuery(id+"F2.opExtrude","CAP_FACE",FACE,{"disambiguationData":[OSD([subQ40])],"isStart":true}),makeQuery(id+"F2.opExtrude","CAP_FACE",FACE,{"disambiguationData":[OSD([subQ39])],"isStart":true}),makeQuery(id+"F2.opExtrude","CAP_FACE",FACE,{"disambiguationData":[OSD([subQ38])],"isStart":true}),makeQuery(id+"F2.opExtrude","CAP_FACE",FACE,{"disambiguationData":[OSD([subQ37])],"isStart":true}),makeQuery(id+"F2.opExtrude","CAP_FACE",FACE,{"disambiguationData":[OSD([subQ36])],"isStart":true}),makeQuery(id+"F2.opExtrude","CAP_FACE",FACE,{"disambiguationData":[OSD([subQ35])],"isStart":true}),makeQuery(id+"F2.opExtrude","CAP_FACE",FACE,{"disambiguationData":[OSD([subQ34])],"isStart":true}),makeQuery(id+"F2.opExtrude","CAP_FACE",FACE,{"disambiguationData":[OSD([subQ33])],"isStart":true}),makeQuery(id+"F2.opExtrude","CAP_FACE",FACE,{"disambiguationData":[OSD([subQ32])],"isStart":true}),makeQuery(id+"F2.opExtrude","CAP_FACE",FACE,{"disambiguationData":[OSD([subQ31])],"isStart":true}),makeQuery(id+"F2.opExtrude","CAP_FACE",FACE,{"disambiguationData":[OSD([subQ30])],"isStart":true}),makeQuery(id+"F2.opExtrude","CAP_FACE",FACE,{"disambiguationData":[OSD([subQ29])],"isStart":true}),makeQuery(id+"F2.opExtrude","CAP_FACE",FACE,{"disambiguationData":[OSD([subQ28])],"isStart":true}),makeQuery(id+"F2.opExtrude","CAP_FACE",FACE,{"disambiguationData":[OSD([subQ27])],"isStart":true}),makeQuery(id+"F2.opExtrude","CAP_FACE",FACE,{"disambiguationData":[OSD([subQ26])],"isStart":true}),makeQuery(id+"F2.opExtrude","CAP_FACE",FACE,{"disambiguationData":[OSD([subQ25])],"isStart":true}),makeQuery(id+"F2.opExtrude","CAP_FACE",FACE,{"disambiguationData":[OSD([subQ24])],"isStart":true}),makeQuery(id+"F2.opExtrude","CAP_FACE",FACE,{"disambiguationData":[OSD([subQ23])],"isStart":true}),makeQuery(id+"F2.opExtrude","CAP_FACE",FACE,{"disambiguationData":[OSD([subQ22])],"isStart":true}),makeQuery(id+"F2.opExtrude","CAP_FACE",FACE,{"disambiguationData":[OSD([subQ21])],"isStart":true}),makeQuery(id+"F2.opExtrude","CAP_FACE",FACE,{"disambiguationData":[OSD([subQ20])],"isStart":true}),makeQuery(id+"F2.opExtrude","CAP_FACE",FACE,{"disambiguationData":[OSD([subQ19])],"isStart":true}),makeQuery(id+"F2.opExtrude","CAP_FACE",FACE,{"disambiguationData":[OSD([subQ18])],"isStart":true}),makeQuery(id+"F2.opExtrude","CAP_FACE",FACE,{"disambiguationData":[OSD([subQ17])],"isStart":true}),makeQuery(id+"F2.opExtrude","CAP_FACE",FACE,{"disambiguationData":[OSD([subQ16])],"isStart":true}),makeQuery(id+"F2.opExtrude","CAP_FACE",FACE,{"disambiguationData":[OSD([subQ15])],"isStart":true}),makeQuery(id+"F2.opExtrude","CAP_FACE",FACE,{"disambiguationData":[OSD([subQ14])],"isStart":true}),makeQuery(id+"F2.opExtrude","CAP_FACE",FACE,{"disambiguationData":[OSD([subQ13])],"isStart":true}),makeQuery(id+"F2.opExtrude","CAP_FACE",FACE,{"disambiguationData":[OSD([subQ12])],"isStart":true}),makeQuery(id+"F2.opExtrude","CAP_FACE",FACE,{"disambiguationData":[OSD([subQ11])],"isStart":true}),makeQuery(id+"F2.opExtrude","CAP_FACE",FACE,{"disambiguationData":[OSD([subQ10])],"isStart":true}),makeQuery(id+"F2.opExtrude","CAP_FACE",FACE,{"disambiguationData":[OSD([subQ9])],"isStart":true}),makeQuery(id+"F2.opExtrude","CAP_FACE",FACE,{"disambiguationData":[OSD([subQ8])],"isStart":true}),makeQuery(id+"F2.opExtrude","CAP_FACE",FACE,{"disambiguationData":[OSD([subQ7])],"isStart":true}),makeQuery(id+"F2.opExtrude","CAP_FACE",FACE,{"disambiguationData":[OSD([subQ6])],"isStart":true}),makeQuery(id+"F2.opExtrude","CAP_FACE",FACE,{"disambiguationData":[OSD([subQ5])],"isStart":true}),makeQuery(id+"F2.opExtrude","CAP_FACE",FACE,{"disambiguationData":[OSD([subQ4])],"isStart":true}),makeQuery(id+"F2.opExtrude","CAP_FACE",FACE,{"disambiguationData":[OSD([subQ3])],"isStart":true}),makeQuery(id+"F2.opExtrude","CAP_FACE",FACE,{"disambiguationData":[OSD([subQ2])],"isStart":true}),makeQuery(id+"F2.opExtrude","CAP_FACE",FACE,{"disambiguationData":[OSD([subQ1])],"isStart":true}),makeQuery(id+"F2.opExtrude","CAP_FACE",FACE,{"disambiguationData":[OSD([subQ0])],"isStart":true})]});}
            shell(context, id + "F3", {"entities" : qUnion([Q0]), "thickness" : 1.59 * mm});
        }
        {
            var Q0;
            Q0=makeQuery(id+"F3.opShell","OFFSET_FACE",FACE,{"disambiguationData":[OSD([sQuery(id+"F0.wireOp",EDGE,"E0.bottom"),sQuery(id+"F0.wireOp",EDGE,"E0.top"),sQuery(id+"F0.wireOp",EDGE,"E0.left"),sQuery(id+"F0.wireOp",EDGE,"E0.right"),sQuery(id+"F0.wireOp",EDGE,"E1"),sQuery(id+"F0.wireOp",EDGE,"E2.0.1.0"),sQuery(id+"F0.wireOp",EDGE,"E2.0.2.0"),sQuery(id+"F0.wireOp",EDGE,"E2.0.3.0"),sQuery(id+"F0.wireOp",EDGE,"E2.0.4.0"),sQuery(id+"F0.wireOp",EDGE,"E2.0.5.0"),sQuery(id+"F0.wireOp",EDGE,"E2.0.6.0"),sQuery(id+"F0.wireOp",EDGE,"E2.0.7.0"),sQuery(id+"F0.wireOp",EDGE,"E2.0.8.0"),sQuery(id+"F0.wireOp",EDGE,"E2.0.9.0"),sQuery(id+"F0.wireOp",EDGE,"E2.1.0.0"),sQuery(id+"F0.wireOp",EDGE,"E2.1.1.0"),sQuery(id+"F0.wireOp",EDGE,"E2.1.2.0"),sQuery(id+"F0.wireOp",EDGE,"E2.1.3.0"),sQuery(id+"F0.wireOp",EDGE,"E2.1.4.0"),sQuery(id+"F0.wireOp",EDGE,"E2.1.5.0"),sQuery(id+"F0.wireOp",EDGE,"E2.1.6.0"),sQuery(id+"F0.wireOp",EDGE,"E2.1.7.0"),sQuery(id+"F0.wireOp",EDGE,"E2.1.8.0"),sQuery(id+"F0.wireOp",EDGE,"E2.1.9.0"),sQuery(id+"F0.wireOp",EDGE,"E2.2.0.0"),sQuery(id+"F0.wireOp",EDGE,"E2.2.1.0"),sQuery(id+"F0.wireOp",EDGE,"E2.2.7.0"),sQuery(id+"F0.wireOp",EDGE,"E2.2.8.0"),sQuery(id+"F0.wireOp",EDGE,"E2.3.0.0"),sQuery(id+"F0.wireOp",EDGE,"E2.3.1.0"),sQuery(id+"F0.wireOp",EDGE,"E2.3.7.0"),sQuery(id+"F0.wireOp",EDGE,"E2.4.0.0"),sQuery(id+"F0.wireOp",EDGE,"E2.4.1.0"),sQuery(id+"F0.wireOp",EDGE,"E2.4.6.0"),sQuery(id+"F0.wireOp",EDGE,"E2.5.0.0"),sQuery(id+"F0.wireOp",EDGE,"E2.5.1.0"),sQuery(id+"F0.wireOp",EDGE,"E2.5.5.0"),sQuery(id+"F0.wireOp",EDGE,"E2.6.0.0"),sQuery(id+"F0.wireOp",EDGE,"E2.6.1.0"),sQuery(id+"F0.wireOp",EDGE,"E2.6.4.0"),sQuery(id+"F0.wireOp",EDGE,"E2.7.0.0"),sQuery(id+"F0.wireOp",EDGE,"E2.7.1.0"),sQuery(id+"F0.wireOp",EDGE,"E2.7.2.0"),sQuery(id+"F0.wireOp",EDGE,"E2.7.3.0"),sQuery(id+"F0.wireOp",EDGE,"E2.8.0.0"),sQuery(id+"F0.wireOp",EDGE,"E2.8.1.0"),sQuery(id+"F0.wireOp",EDGE,"E2.8.2.0"),sQuery(id+"F0.wireOp",EDGE,"E2.9.0.0"),sQuery(id+"F0.wireOp",EDGE,"E2.9.1.0"),sQuery(id+"F0.wireOp",EDGE,"E5")])]});
            var sketch = newSketch(context, id + "F4", { "sketchPlane" : qUnion([Q0])});
            skLineSegment(sketch, "E6", {"start": v(-35.72, 35.72) * mm, "end": v(-27.78, 27.78) * mm});
            skCircle(sketch, "E7", {"center": v(-31.75, 31.75) * mm, "radius": 3.18 * mm});
            skCircle(sketch, "E8.0", {"center": v(-31.75, 31.75) * mm, "radius": 2.38 * mm});
            skCircle(sketch, "E9.0.1.0", {"center": v(-31.75, 23.81) * mm, "radius": 3.18 * mm});
            skCircle(sketch, "E9.0.1.1", {"center": v(-31.75, 23.81) * mm, "radius": 2.38 * mm});
            skCircle(sketch, "E9.0.2.0", {"center": v(-31.75, 15.88) * mm, "radius": 3.18 * mm});
            skCircle(sketch, "E9.0.2.1", {"center": v(-31.75, 15.88) * mm, "radius": 2.38 * mm});
            skCircle(sketch, "E9.0.3.0", {"center": v(-31.75, 7.94) * mm, "radius": 3.18 * mm});
            skCircle(sketch, "E9.0.3.1", {"center": v(-31.75, 7.94) * mm, "radius": 2.38 * mm});
            skCircle(sketch, "E9.0.4.0", {"center": v(-31.75, 0) * mm, "radius": 3.18 * mm});
            skCircle(sketch, "E9.0.4.1", {"center": v(-31.75, 0) * mm, "radius": 2.38 * mm});
            skCircle(sketch, "E9.0.5.0", {"center": v(-31.75, -7.94) * mm, "radius": 3.18 * mm});
            skCircle(sketch, "E9.0.5.1", {"center": v(-31.75, -7.94) * mm, "radius": 2.38 * mm});
            skCircle(sketch, "E9.0.6.0", {"center": v(-31.75, -15.87) * mm, "radius": 3.18 * mm});
            skCircle(sketch, "E9.0.6.1", {"center": v(-31.75, -15.87) * mm, "radius": 2.38 * mm});
            skCircle(sketch, "E9.0.7.0", {"center": v(-31.75, -23.81) * mm, "radius": 3.18 * mm});
            skCircle(sketch, "E9.0.7.1", {"center": v(-31.75, -23.81) * mm, "radius": 2.38 * mm});
            skCircle(sketch, "E9.0.8.0", {"center": v(-31.75, -31.75) * mm, "radius": 3.18 * mm});
            skCircle(sketch, "E9.0.8.1", {"center": v(-31.75, -31.75) * mm, "radius": 2.38 * mm});
            skCircle(sketch, "E9.1.0.0", {"center": v(-23.81, 31.75) * mm, "radius": 3.18 * mm});
            skCircle(sketch, "E9.1.0.1", {"center": v(-23.81, 31.75) * mm, "radius": 2.38 * mm});
            skCircle(sketch, "E9.1.1.0", {"center": v(-23.81, 23.81) * mm, "radius": 3.18 * mm});
            skCircle(sketch, "E9.1.1.1", {"center": v(-23.81, 23.81) * mm, "radius": 2.38 * mm});
            skCircle(sketch, "E9.1.2.0", {"center": v(-23.81, 15.88) * mm, "radius": 3.18 * mm});
            skCircle(sketch, "E9.1.2.1", {"center": v(-23.81, 15.88) * mm, "radius": 2.38 * mm});
            skCircle(sketch, "E9.1.3.0", {"center": v(-23.81, 7.94) * mm, "radius": 3.18 * mm});
            skCircle(sketch, "E9.1.3.1", {"center": v(-23.81, 7.94) * mm, "radius": 2.38 * mm});
            skCircle(sketch, "E9.1.4.0", {"center": v(-23.81, 0) * mm, "radius": 3.18 * mm});
            skCircle(sketch, "E9.1.4.1", {"center": v(-23.81, 0) * mm, "radius": 2.38 * mm});
            skCircle(sketch, "E9.1.5.0", {"center": v(-23.81, -7.94) * mm, "radius": 3.18 * mm});
            skCircle(sketch, "E9.1.5.1", {"center": v(-23.81, -7.94) * mm, "radius": 2.38 * mm});
            skCircle(sketch, "E9.1.6.0", {"center": v(-23.81, -15.87) * mm, "radius": 3.18 * mm});
            skCircle(sketch, "E9.1.6.1", {"center": v(-23.81, -15.87) * mm, "radius": 2.38 * mm});
            skCircle(sketch, "E9.1.7.0", {"center": v(-23.81, -23.81) * mm, "radius": 3.18 * mm});
            skCircle(sketch, "E9.1.7.1", {"center": v(-23.81, -23.81) * mm, "radius": 2.38 * mm});
            skCircle(sketch, "E9.1.8.0", {"center": v(-23.81, -31.75) * mm, "radius": 3.18 * mm});
            skCircle(sketch, "E9.1.8.1", {"center": v(-23.81, -31.75) * mm, "radius": 2.38 * mm});
            skCircle(sketch, "E9.2.0.0", {"center": v(-15.88, 31.75) * mm, "radius": 3.18 * mm});
            skCircle(sketch, "E9.2.0.1", {"center": v(-15.88, 31.75) * mm, "radius": 2.38 * mm});
            skCircle(sketch, "E9.2.1.0", {"center": v(-15.88, 23.81) * mm, "radius": 3.18 * mm});
            skCircle(sketch, "E9.2.1.1", {"center": v(-15.88, 23.81) * mm, "radius": 2.38 * mm});
            skCircle(sketch, "E9.2.2.0", {"center": v(-15.88, 15.88) * mm, "radius": 3.18 * mm});
            skCircle(sketch, "E9.2.2.1", {"center": v(-15.88, 15.88) * mm, "radius": 2.38 * mm});
            skCircle(sketch, "E9.2.3.0", {"center": v(-15.88, 7.94) * mm, "radius": 3.18 * mm});
            skCircle(sketch, "E9.2.3.1", {"center": v(-15.88, 7.94) * mm, "radius": 2.38 * mm});
            skCircle(sketch, "E9.2.4.0", {"center": v(-15.88, 0) * mm, "radius": 3.18 * mm});
            skCircle(sketch, "E9.2.4.1", {"center": v(-15.88, 0) * mm, "radius": 2.38 * mm});
            skCircle(sketch, "E9.2.5.0", {"center": v(-15.88, -7.94) * mm, "radius": 3.18 * mm});
            skCircle(sketch, "E9.2.5.1", {"center": v(-15.88, -7.94) * mm, "radius": 2.38 * mm});
            skCircle(sketch, "E9.2.6.0", {"center": v(-15.88, -15.87) * mm, "radius": 3.18 * mm});
            skCircle(sketch, "E9.2.6.1", {"center": v(-15.88, -15.87) * mm, "radius": 2.38 * mm});
            skCircle(sketch, "E9.2.7.0", {"center": v(-15.88, -23.81) * mm, "radius": 3.18 * mm});
            skCircle(sketch, "E9.2.7.1", {"center": v(-15.88, -23.81) * mm, "radius": 2.38 * mm});
            skCircle(sketch, "E9.2.8.0", {"center": v(-15.88, -31.75) * mm, "radius": 3.18 * mm});
            skCircle(sketch, "E9.2.8.1", {"center": v(-15.88, -31.75) * mm, "radius": 2.38 * mm});
            skCircle(sketch, "E9.3.0.0", {"center": v(-7.94, 31.75) * mm, "radius": 3.18 * mm});
            skCircle(sketch, "E9.3.0.1", {"center": v(-7.94, 31.75) * mm, "radius": 2.38 * mm});
            skCircle(sketch, "E9.3.1.0", {"center": v(-7.94, 23.81) * mm, "radius": 3.18 * mm});
            skCircle(sketch, "E9.3.1.1", {"center": v(-7.94, 23.81) * mm, "radius": 2.38 * mm});
            skCircle(sketch, "E9.3.2.0", {"center": v(-7.94, 15.88) * mm, "radius": 3.18 * mm});
            skCircle(sketch, "E9.3.2.1", {"center": v(-7.94, 15.88) * mm, "radius": 2.38 * mm});
            skCircle(sketch, "E9.3.3.0", {"center": v(-7.94, 7.94) * mm, "radius": 3.18 * mm});
            skCircle(sketch, "E9.3.3.1", {"center": v(-7.94, 7.94) * mm, "radius": 2.38 * mm});
            skCircle(sketch, "E9.3.4.0", {"center": v(-7.94, 0) * mm, "radius": 3.18 * mm});
            skCircle(sketch, "E9.3.4.1", {"center": v(-7.94, 0) * mm, "radius": 2.38 * mm});
            skCircle(sketch, "E9.3.5.0", {"center": v(-7.94, -7.94) * mm, "radius": 3.18 * mm});
            skCircle(sketch, "E9.3.5.1", {"center": v(-7.94, -7.94) * mm, "radius": 2.38 * mm});
            skCircle(sketch, "E9.3.6.0", {"center": v(-7.94, -15.87) * mm, "radius": 3.18 * mm});
            skCircle(sketch, "E9.3.6.1", {"center": v(-7.94, -15.87) * mm, "radius": 2.38 * mm});
            skCircle(sketch, "E9.3.7.0", {"center": v(-7.94, -23.81) * mm, "radius": 3.18 * mm});
            skCircle(sketch, "E9.3.7.1", {"center": v(-7.94, -23.81) * mm, "radius": 2.38 * mm});
            skCircle(sketch, "E9.3.8.0", {"center": v(-7.94, -31.75) * mm, "radius": 3.18 * mm});
            skCircle(sketch, "E9.3.8.1", {"center": v(-7.94, -31.75) * mm, "radius": 2.38 * mm});
            skCircle(sketch, "E9.4.0.0", {"center": v(0, 31.75) * mm, "radius": 3.18 * mm});
            skCircle(sketch, "E9.4.0.1", {"center": v(0, 31.75) * mm, "radius": 2.38 * mm});
            skCircle(sketch, "E9.4.1.0", {"center": v(0, 23.81) * mm, "radius": 3.18 * mm});
            skCircle(sketch, "E9.4.1.1", {"center": v(0, 23.81) * mm, "radius": 2.38 * mm});
            skCircle(sketch, "E9.4.2.0", {"center": v(0, 15.88) * mm, "radius": 3.18 * mm});
            skCircle(sketch, "E9.4.2.1", {"center": v(0, 15.88) * mm, "radius": 2.38 * mm});
            skCircle(sketch, "E9.4.3.0", {"center": v(0, 7.94) * mm, "radius": 3.18 * mm});
            skCircle(sketch, "E9.4.3.1", {"center": v(0, 7.94) * mm, "radius": 2.38 * mm});
            skCircle(sketch, "E9.4.4.0", {"center": v(0, 0) * mm, "radius": 3.18 * mm});
            skCircle(sketch, "E9.4.4.1", {"center": v(0, 0) * mm, "radius": 2.38 * mm});
            skCircle(sketch, "E9.4.5.0", {"center": v(0, -7.94) * mm, "radius": 3.18 * mm});
            skCircle(sketch, "E9.4.5.1", {"center": v(0, -7.94) * mm, "radius": 2.38 * mm});
            skCircle(sketch, "E9.4.6.0", {"center": v(0, -15.87) * mm, "radius": 3.18 * mm});
            skCircle(sketch, "E9.4.6.1", {"center": v(0, -15.87) * mm, "radius": 2.38 * mm});
            skCircle(sketch, "E9.4.7.0", {"center": v(0, -23.81) * mm, "radius": 3.18 * mm});
            skCircle(sketch, "E9.4.7.1", {"center": v(0, -23.81) * mm, "radius": 2.38 * mm});
            skCircle(sketch, "E9.4.8.0", {"center": v(0, -31.75) * mm, "radius": 3.18 * mm});
            skCircle(sketch, "E9.4.8.1", {"center": v(0, -31.75) * mm, "radius": 2.38 * mm});
            skCircle(sketch, "E9.5.0.0", {"center": v(7.94, 31.75) * mm, "radius": 3.18 * mm});
            skCircle(sketch, "E9.5.0.1", {"center": v(7.94, 31.75) * mm, "radius": 2.38 * mm});
            skCircle(sketch, "E9.5.1.0", {"center": v(7.94, 23.81) * mm, "radius": 3.18 * mm});
            skCircle(sketch, "E9.5.1.1", {"center": v(7.94, 23.81) * mm, "radius": 2.38 * mm});
            skCircle(sketch, "E9.5.2.0", {"center": v(7.94, 15.88) * mm, "radius": 3.18 * mm});
            skCircle(sketch, "E9.5.2.1", {"center": v(7.94, 15.88) * mm, "radius": 2.38 * mm});
            skCircle(sketch, "E9.5.3.0", {"center": v(7.94, 7.94) * mm, "radius": 3.18 * mm});
            skCircle(sketch, "E9.5.3.1", {"center": v(7.94, 7.94) * mm, "radius": 2.38 * mm});
            skCircle(sketch, "E9.5.4.0", {"center": v(7.94, 0) * mm, "radius": 3.18 * mm});
            skCircle(sketch, "E9.5.4.1", {"center": v(7.94, 0) * mm, "radius": 2.38 * mm});
            skCircle(sketch, "E9.5.5.0", {"center": v(7.94, -7.94) * mm, "radius": 3.18 * mm});
            skCircle(sketch, "E9.5.5.1", {"center": v(7.94, -7.94) * mm, "radius": 2.38 * mm});
            skCircle(sketch, "E9.5.6.0", {"center": v(7.94, -15.87) * mm, "radius": 3.18 * mm});
            skCircle(sketch, "E9.5.6.1", {"center": v(7.94, -15.87) * mm, "radius": 2.38 * mm});
            skCircle(sketch, "E9.5.7.0", {"center": v(7.94, -23.81) * mm, "radius": 3.18 * mm});
            skCircle(sketch, "E9.5.7.1", {"center": v(7.94, -23.81) * mm, "radius": 2.38 * mm});
            skCircle(sketch, "E9.5.8.0", {"center": v(7.94, -31.75) * mm, "radius": 3.18 * mm});
            skCircle(sketch, "E9.5.8.1", {"center": v(7.94, -31.75) * mm, "radius": 2.38 * mm});
            skCircle(sketch, "E9.6.0.0", {"center": v(15.87, 31.75) * mm, "radius": 3.18 * mm});
            skCircle(sketch, "E9.6.0.1", {"center": v(15.87, 31.75) * mm, "radius": 2.38 * mm});
            skCircle(sketch, "E9.6.1.0", {"center": v(15.87, 23.81) * mm, "radius": 3.18 * mm});
            skCircle(sketch, "E9.6.1.1", {"center": v(15.87, 23.81) * mm, "radius": 2.38 * mm});
            skCircle(sketch, "E9.6.2.0", {"center": v(15.87, 15.88) * mm, "radius": 3.18 * mm});
            skCircle(sketch, "E9.6.2.1", {"center": v(15.87, 15.88) * mm, "radius": 2.38 * mm});
            skCircle(sketch, "E9.6.3.0", {"center": v(15.87, 7.94) * mm, "radius": 3.18 * mm});
            skCircle(sketch, "E9.6.3.1", {"center": v(15.87, 7.94) * mm, "radius": 2.38 * mm});
            skCircle(sketch, "E9.6.4.0", {"center": v(15.87, 0) * mm, "radius": 3.18 * mm});
            skCircle(sketch, "E9.6.4.1", {"center": v(15.87, 0) * mm, "radius": 2.38 * mm});
            skCircle(sketch, "E9.6.5.0", {"center": v(15.87, -7.94) * mm, "radius": 3.18 * mm});
            skCircle(sketch, "E9.6.5.1", {"center": v(15.87, -7.94) * mm, "radius": 2.38 * mm});
            skCircle(sketch, "E9.6.6.0", {"center": v(15.87, -15.87) * mm, "radius": 3.18 * mm});
            skCircle(sketch, "E9.6.6.1", {"center": v(15.87, -15.87) * mm, "radius": 2.38 * mm});
            skCircle(sketch, "E9.6.7.0", {"center": v(15.87, -23.81) * mm, "radius": 3.18 * mm});
            skCircle(sketch, "E9.6.7.1", {"center": v(15.87, -23.81) * mm, "radius": 2.38 * mm});
            skCircle(sketch, "E9.6.8.0", {"center": v(15.87, -31.75) * mm, "radius": 3.18 * mm});
            skCircle(sketch, "E9.6.8.1", {"center": v(15.87, -31.75) * mm, "radius": 2.38 * mm});
            skCircle(sketch, "E9.7.0.0", {"center": v(23.81, 31.75) * mm, "radius": 3.18 * mm});
            skCircle(sketch, "E9.7.0.1", {"center": v(23.81, 31.75) * mm, "radius": 2.38 * mm});
            skCircle(sketch, "E9.7.1.0", {"center": v(23.81, 23.81) * mm, "radius": 3.18 * mm});
            skCircle(sketch, "E9.7.1.1", {"center": v(23.81, 23.81) * mm, "radius": 2.38 * mm});
            skCircle(sketch, "E9.7.2.0", {"center": v(23.81, 15.88) * mm, "radius": 3.18 * mm});
            skCircle(sketch, "E9.7.2.1", {"center": v(23.81, 15.88) * mm, "radius": 2.38 * mm});
            skCircle(sketch, "E9.7.3.0", {"center": v(23.81, 7.94) * mm, "radius": 3.18 * mm});
            skCircle(sketch, "E9.7.3.1", {"center": v(23.81, 7.94) * mm, "radius": 2.38 * mm});
            skCircle(sketch, "E9.7.4.0", {"center": v(23.81, 0) * mm, "radius": 3.18 * mm});
            skCircle(sketch, "E9.7.4.1", {"center": v(23.81, 0) * mm, "radius": 2.38 * mm});
            skCircle(sketch, "E9.7.5.0", {"center": v(23.81, -7.94) * mm, "radius": 3.18 * mm});
            skCircle(sketch, "E9.7.5.1", {"center": v(23.81, -7.94) * mm, "radius": 2.38 * mm});
            skCircle(sketch, "E9.7.6.0", {"center": v(23.81, -15.87) * mm, "radius": 3.18 * mm});
            skCircle(sketch, "E9.7.6.1", {"center": v(23.81, -15.87) * mm, "radius": 2.38 * mm});
            skCircle(sketch, "E9.7.7.0", {"center": v(23.81, -23.81) * mm, "radius": 3.18 * mm});
            skCircle(sketch, "E9.7.7.1", {"center": v(23.81, -23.81) * mm, "radius": 2.38 * mm});
            skCircle(sketch, "E9.7.8.0", {"center": v(23.81, -31.75) * mm, "radius": 3.18 * mm});
            skCircle(sketch, "E9.7.8.1", {"center": v(23.81, -31.75) * mm, "radius": 2.38 * mm});
            skCircle(sketch, "E9.8.0.0", {"center": v(31.75, 31.75) * mm, "radius": 3.18 * mm});
            skCircle(sketch, "E9.8.0.1", {"center": v(31.75, 31.75) * mm, "radius": 2.38 * mm});
            skCircle(sketch, "E9.8.1.0", {"center": v(31.75, 23.81) * mm, "radius": 3.18 * mm});
            skCircle(sketch, "E9.8.1.1", {"center": v(31.75, 23.81) * mm, "radius": 2.38 * mm});
            skCircle(sketch, "E9.8.2.0", {"center": v(31.75, 15.88) * mm, "radius": 3.18 * mm});
            skCircle(sketch, "E9.8.2.1", {"center": v(31.75, 15.88) * mm, "radius": 2.38 * mm});
            skCircle(sketch, "E9.8.3.0", {"center": v(31.75, 7.94) * mm, "radius": 3.18 * mm});
            skCircle(sketch, "E9.8.3.1", {"center": v(31.75, 7.94) * mm, "radius": 2.38 * mm});
            skCircle(sketch, "E9.8.4.0", {"center": v(31.75, 0) * mm, "radius": 3.18 * mm});
            skCircle(sketch, "E9.8.4.1", {"center": v(31.75, 0) * mm, "radius": 2.38 * mm});
            skCircle(sketch, "E9.8.5.0", {"center": v(31.75, -7.94) * mm, "radius": 3.18 * mm});
            skCircle(sketch, "E9.8.5.1", {"center": v(31.75, -7.94) * mm, "radius": 2.38 * mm});
            skCircle(sketch, "E9.8.6.0", {"center": v(31.75, -15.87) * mm, "radius": 3.18 * mm});
            skCircle(sketch, "E9.8.6.1", {"center": v(31.75, -15.87) * mm, "radius": 2.38 * mm});
            skCircle(sketch, "E9.8.7.0", {"center": v(31.75, -23.81) * mm, "radius": 3.18 * mm});
            skCircle(sketch, "E9.8.7.1", {"center": v(31.75, -23.81) * mm, "radius": 2.38 * mm});
            skCircle(sketch, "E9.8.8.0", {"center": v(31.75, -31.75) * mm, "radius": 3.18 * mm});
            skCircle(sketch, "E9.8.8.1", {"center": v(31.75, -31.75) * mm, "radius": 2.38 * mm});
            skLineSegment(sketch, "E9.direction1", {"start": v(-31.75, 31.75) * mm, "end": v(-23.81, 31.75) * mm, "construction": true});
            skLineSegment(sketch, "E9.direction2", {"start": v(-31.75, 31.75) * mm, "end": v(-31.75, 23.81) * mm, "construction": true});
            skSolve(sketch);
        }
        {
            var Q0;
            Q0=makeQuery(id+"F4.imprint","IMPRINT",FACE,{"disambiguationData":[TD([[makeQuery(id+"F4.imprint","IMPRINT",EDGE,{"derivedFrom":sQuery(id+"F4.wireOp",EDGE,"E9.0.1.0")}),1.0]])]});
            var Q1;
            Q1=makeQuery(id+"F4.imprint","IMPRINT",FACE,{"disambiguationData":[TD([[makeQuery(id+"F4.imprint","IMPRINT",EDGE,{"derivedFrom":sQuery(id+"F4.wireOp",EDGE,"E9.0.2.0")}),1.0]])]});
            var Q2;
            Q2=makeQuery(id+"F4.imprint","IMPRINT",FACE,{"disambiguationData":[TD([[makeQuery(id+"F4.imprint","IMPRINT",EDGE,{"derivedFrom":sQuery(id+"F4.wireOp",EDGE,"E9.0.3.0")}),1.0]])]});
            var Q3;
            Q3=makeQuery(id+"F4.imprint","IMPRINT",FACE,{"disambiguationData":[TD([[makeQuery(id+"F4.imprint","IMPRINT",EDGE,{"derivedFrom":sQuery(id+"F4.wireOp",EDGE,"E9.0.4.0")}),1.0]])]});
            var Q4;
            Q4=makeQuery(id+"F4.imprint","IMPRINT",FACE,{"disambiguationData":[TD([[makeQuery(id+"F4.imprint","IMPRINT",EDGE,{"derivedFrom":sQuery(id+"F4.wireOp",EDGE,"E9.0.5.0")}),1.0]])]});
            var Q5;
            Q5=makeQuery(id+"F4.imprint","IMPRINT",FACE,{"disambiguationData":[TD([[makeQuery(id+"F4.imprint","IMPRINT",EDGE,{"derivedFrom":sQuery(id+"F4.wireOp",EDGE,"E9.0.6.0")}),1.0]])]});
            var Q6;
            Q6=makeQuery(id+"F4.imprint","IMPRINT",FACE,{"disambiguationData":[TD([[makeQuery(id+"F4.imprint","IMPRINT",EDGE,{"derivedFrom":sQuery(id+"F4.wireOp",EDGE,"E9.0.7.0")}),1.0]])]});
            var Q7;
            Q7=makeQuery(id+"F4.imprint","IMPRINT",FACE,{"disambiguationData":[TD([[makeQuery(id+"F4.imprint","IMPRINT",EDGE,{"derivedFrom":sQuery(id+"F4.wireOp",EDGE,"E9.0.8.0")}),1.0]])]});
            var Q8;
            Q8=makeQuery(id+"F4.imprint","IMPRINT",FACE,{"disambiguationData":[TD([[makeQuery(id+"F4.imprint","IMPRINT",EDGE,{"derivedFrom":sQuery(id+"F4.wireOp",EDGE,"E9.1.0.0")}),1.0]])]});
            var Q9;
            Q9=makeQuery(id+"F4.imprint","IMPRINT",FACE,{"disambiguationData":[TD([[makeQuery(id+"F4.imprint","IMPRINT",EDGE,{"derivedFrom":sQuery(id+"F4.wireOp",EDGE,"E9.1.1.0")}),1.0]])]});
            var Q10;
            Q10=makeQuery(id+"F4.imprint","IMPRINT",FACE,{"disambiguationData":[TD([[makeQuery(id+"F4.imprint","IMPRINT",EDGE,{"derivedFrom":sQuery(id+"F4.wireOp",EDGE,"E9.1.2.0")}),1.0]])]});
            var Q11;
            Q11=makeQuery(id+"F4.imprint","IMPRINT",FACE,{"disambiguationData":[TD([[makeQuery(id+"F4.imprint","IMPRINT",EDGE,{"derivedFrom":sQuery(id+"F4.wireOp",EDGE,"E9.1.3.0")}),1.0]])]});
            var Q12;
            Q12=makeQuery(id+"F4.imprint","IMPRINT",FACE,{"disambiguationData":[TD([[makeQuery(id+"F4.imprint","IMPRINT",EDGE,{"derivedFrom":sQuery(id+"F4.wireOp",EDGE,"E9.1.4.0")}),1.0]])]});
            var Q13;
            Q13=makeQuery(id+"F4.imprint","IMPRINT",FACE,{"disambiguationData":[TD([[makeQuery(id+"F4.imprint","IMPRINT",EDGE,{"derivedFrom":sQuery(id+"F4.wireOp",EDGE,"E9.1.5.0")}),1.0]])]});
            var Q14;
            Q14=makeQuery(id+"F4.imprint","IMPRINT",FACE,{"disambiguationData":[TD([[makeQuery(id+"F4.imprint","IMPRINT",EDGE,{"derivedFrom":sQuery(id+"F4.wireOp",EDGE,"E9.1.6.0")}),1.0]])]});
            var Q15;
            Q15=makeQuery(id+"F4.imprint","IMPRINT",FACE,{"disambiguationData":[TD([[makeQuery(id+"F4.imprint","IMPRINT",EDGE,{"derivedFrom":sQuery(id+"F4.wireOp",EDGE,"E9.1.7.0")}),1.0]])]});
            var Q16;
            Q16=makeQuery(id+"F4.imprint","IMPRINT",FACE,{"disambiguationData":[TD([[makeQuery(id+"F4.imprint","IMPRINT",EDGE,{"derivedFrom":sQuery(id+"F4.wireOp",EDGE,"E9.1.8.0")}),1.0]])]});
            var Q17;
            Q17=makeQuery(id+"F4.imprint","IMPRINT",FACE,{"disambiguationData":[TD([[makeQuery(id+"F4.imprint","IMPRINT",EDGE,{"derivedFrom":sQuery(id+"F4.wireOp",EDGE,"E9.2.0.0")}),1.0]])]});
            var Q18;
            Q18=makeQuery(id+"F4.imprint","IMPRINT",FACE,{"disambiguationData":[TD([[makeQuery(id+"F4.imprint","IMPRINT",EDGE,{"derivedFrom":sQuery(id+"F4.wireOp",EDGE,"E9.2.1.0")}),1.0]])]});
            var Q19;
            Q19=makeQuery(id+"F4.imprint","IMPRINT",FACE,{"disambiguationData":[TD([[makeQuery(id+"F4.imprint","IMPRINT",EDGE,{"derivedFrom":sQuery(id+"F4.wireOp",EDGE,"E9.2.2.0")}),1.0]])]});
            var Q20;
            Q20=makeQuery(id+"F4.imprint","IMPRINT",FACE,{"disambiguationData":[TD([[makeQuery(id+"F4.imprint","IMPRINT",EDGE,{"derivedFrom":sQuery(id+"F4.wireOp",EDGE,"E9.2.3.0")}),1.0]])]});
            var Q21;
            Q21=makeQuery(id+"F4.imprint","IMPRINT",FACE,{"disambiguationData":[TD([[makeQuery(id+"F4.imprint","IMPRINT",EDGE,{"derivedFrom":sQuery(id+"F4.wireOp",EDGE,"E9.2.4.0")}),1.0]])]});
            var Q22;
            Q22=makeQuery(id+"F4.imprint","IMPRINT",FACE,{"disambiguationData":[TD([[makeQuery(id+"F4.imprint","IMPRINT",EDGE,{"derivedFrom":sQuery(id+"F4.wireOp",EDGE,"E9.2.5.0")}),1.0]])]});
            var Q23;
            Q23=makeQuery(id+"F4.imprint","IMPRINT",FACE,{"disambiguationData":[TD([[makeQuery(id+"F4.imprint","IMPRINT",EDGE,{"derivedFrom":sQuery(id+"F4.wireOp",EDGE,"E9.2.6.0")}),1.0]])]});
            var Q24;
            Q24=makeQuery(id+"F4.imprint","IMPRINT",FACE,{"disambiguationData":[TD([[makeQuery(id+"F4.imprint","IMPRINT",EDGE,{"derivedFrom":sQuery(id+"F4.wireOp",EDGE,"E9.2.7.0")}),1.0]])]});
            var Q25;
            Q25=makeQuery(id+"F4.imprint","IMPRINT",FACE,{"disambiguationData":[TD([[makeQuery(id+"F4.imprint","IMPRINT",EDGE,{"derivedFrom":sQuery(id+"F4.wireOp",EDGE,"E9.3.0.0")}),1.0]])]});
            var Q26;
            Q26=makeQuery(id+"F4.imprint","IMPRINT",FACE,{"disambiguationData":[TD([[makeQuery(id+"F4.imprint","IMPRINT",EDGE,{"derivedFrom":sQuery(id+"F4.wireOp",EDGE,"E9.3.1.0")}),1.0]])]});
            var Q27;
            Q27=makeQuery(id+"F4.imprint","IMPRINT",FACE,{"disambiguationData":[TD([[makeQuery(id+"F4.imprint","IMPRINT",EDGE,{"derivedFrom":sQuery(id+"F4.wireOp",EDGE,"E9.3.2.0")}),1.0]])]});
            var Q28;
            Q28=makeQuery(id+"F4.imprint","IMPRINT",FACE,{"disambiguationData":[TD([[makeQuery(id+"F4.imprint","IMPRINT",EDGE,{"derivedFrom":sQuery(id+"F4.wireOp",EDGE,"E9.3.3.0")}),1.0]])]});
            var Q29;
            Q29=makeQuery(id+"F4.imprint","IMPRINT",FACE,{"disambiguationData":[TD([[makeQuery(id+"F4.imprint","IMPRINT",EDGE,{"derivedFrom":sQuery(id+"F4.wireOp",EDGE,"E9.3.4.0")}),1.0]])]});
            var Q30;
            Q30=makeQuery(id+"F4.imprint","IMPRINT",FACE,{"disambiguationData":[TD([[makeQuery(id+"F4.imprint","IMPRINT",EDGE,{"derivedFrom":sQuery(id+"F4.wireOp",EDGE,"E9.3.5.0")}),1.0]])]});
            var Q31;
            Q31=makeQuery(id+"F4.imprint","IMPRINT",FACE,{"disambiguationData":[TD([[makeQuery(id+"F4.imprint","IMPRINT",EDGE,{"derivedFrom":sQuery(id+"F4.wireOp",EDGE,"E9.3.6.0")}),1.0]])]});
            var Q32;
            Q32=makeQuery(id+"F4.imprint","IMPRINT",FACE,{"disambiguationData":[TD([[makeQuery(id+"F4.imprint","IMPRINT",EDGE,{"derivedFrom":sQuery(id+"F4.wireOp",EDGE,"E9.4.0.0")}),1.0]])]});
            var Q33;
            Q33=makeQuery(id+"F4.imprint","IMPRINT",FACE,{"disambiguationData":[TD([[makeQuery(id+"F4.imprint","IMPRINT",EDGE,{"derivedFrom":sQuery(id+"F4.wireOp",EDGE,"E9.4.1.0")}),1.0]])]});
            var Q34;
            Q34=makeQuery(id+"F4.imprint","IMPRINT",FACE,{"disambiguationData":[TD([[makeQuery(id+"F4.imprint","IMPRINT",EDGE,{"derivedFrom":sQuery(id+"F4.wireOp",EDGE,"E9.4.2.0")}),1.0]])]});
            var Q35;
            Q35=makeQuery(id+"F4.imprint","IMPRINT",FACE,{"disambiguationData":[TD([[makeQuery(id+"F4.imprint","IMPRINT",EDGE,{"derivedFrom":sQuery(id+"F4.wireOp",EDGE,"E9.4.3.0")}),1.0]])]});
            var Q36;
            Q36=makeQuery(id+"F4.imprint","IMPRINT",FACE,{"disambiguationData":[TD([[makeQuery(id+"F4.imprint","IMPRINT",EDGE,{"derivedFrom":sQuery(id+"F4.wireOp",EDGE,"E9.4.4.0")}),1.0]])]});
            var Q37;
            Q37=makeQuery(id+"F4.imprint","IMPRINT",FACE,{"disambiguationData":[TD([[makeQuery(id+"F4.imprint","IMPRINT",EDGE,{"derivedFrom":sQuery(id+"F4.wireOp",EDGE,"E9.4.5.0")}),1.0]])]});
            var Q38;
            Q38=makeQuery(id+"F4.imprint","IMPRINT",FACE,{"disambiguationData":[TD([[makeQuery(id+"F4.imprint","IMPRINT",EDGE,{"derivedFrom":sQuery(id+"F4.wireOp",EDGE,"E9.5.0.0")}),1.0]])]});
            var Q39;
            Q39=makeQuery(id+"F4.imprint","IMPRINT",FACE,{"disambiguationData":[TD([[makeQuery(id+"F4.imprint","IMPRINT",EDGE,{"derivedFrom":sQuery(id+"F4.wireOp",EDGE,"E9.5.1.0")}),1.0]])]});
            var Q40;
            Q40=makeQuery(id+"F4.imprint","IMPRINT",FACE,{"disambiguationData":[TD([[makeQuery(id+"F4.imprint","IMPRINT",EDGE,{"derivedFrom":sQuery(id+"F4.wireOp",EDGE,"E9.5.2.0")}),1.0]])]});
            var Q41;
            Q41=makeQuery(id+"F4.imprint","IMPRINT",FACE,{"disambiguationData":[TD([[makeQuery(id+"F4.imprint","IMPRINT",EDGE,{"derivedFrom":sQuery(id+"F4.wireOp",EDGE,"E9.5.3.0")}),1.0]])]});
            var Q42;
            Q42=makeQuery(id+"F4.imprint","IMPRINT",FACE,{"disambiguationData":[TD([[makeQuery(id+"F4.imprint","IMPRINT",EDGE,{"derivedFrom":sQuery(id+"F4.wireOp",EDGE,"E9.5.4.0")}),1.0]])]});
            var Q43;
            Q43=makeQuery(id+"F4.imprint","IMPRINT",FACE,{"disambiguationData":[TD([[makeQuery(id+"F4.imprint","IMPRINT",EDGE,{"derivedFrom":sQuery(id+"F4.wireOp",EDGE,"E9.6.0.0")}),1.0]])]});
            var Q44;
            Q44=makeQuery(id+"F4.imprint","IMPRINT",FACE,{"disambiguationData":[TD([[makeQuery(id+"F4.imprint","IMPRINT",EDGE,{"derivedFrom":sQuery(id+"F4.wireOp",EDGE,"E9.6.1.0")}),1.0]])]});
            var Q45;
            Q45=makeQuery(id+"F4.imprint","IMPRINT",FACE,{"disambiguationData":[TD([[makeQuery(id+"F4.imprint","IMPRINT",EDGE,{"derivedFrom":sQuery(id+"F4.wireOp",EDGE,"E9.6.2.0")}),1.0]])]});
            var Q46;
            Q46=makeQuery(id+"F4.imprint","IMPRINT",FACE,{"disambiguationData":[TD([[makeQuery(id+"F4.imprint","IMPRINT",EDGE,{"derivedFrom":sQuery(id+"F4.wireOp",EDGE,"E9.6.3.0")}),1.0]])]});
            var Q47;
            Q47=makeQuery(id+"F4.imprint","IMPRINT",FACE,{"disambiguationData":[TD([[makeQuery(id+"F4.imprint","IMPRINT",EDGE,{"derivedFrom":sQuery(id+"F4.wireOp",EDGE,"E9.7.0.0")}),1.0]])]});
            var Q48;
            Q48=makeQuery(id+"F4.imprint","IMPRINT",FACE,{"disambiguationData":[TD([[makeQuery(id+"F4.imprint","IMPRINT",EDGE,{"derivedFrom":sQuery(id+"F4.wireOp",EDGE,"E9.7.1.0")}),1.0]])]});
            var Q49;
            Q49=makeQuery(id+"F4.imprint","IMPRINT",FACE,{"disambiguationData":[TD([[makeQuery(id+"F4.imprint","IMPRINT",EDGE,{"derivedFrom":sQuery(id+"F4.wireOp",EDGE,"E9.7.2.0")}),1.0]])]});
            var Q50;
            Q50=makeQuery(id+"F4.imprint","IMPRINT",FACE,{"disambiguationData":[TD([[makeQuery(id+"F4.imprint","IMPRINT",EDGE,{"derivedFrom":sQuery(id+"F4.wireOp",EDGE,"E9.8.0.0")}),1.0]])]});
            var Q51;
            Q51=makeQuery(id+"F4.imprint","IMPRINT",FACE,{"disambiguationData":[TD([[makeQuery(id+"F4.imprint","IMPRINT",EDGE,{"derivedFrom":sQuery(id+"F4.wireOp",EDGE,"E9.8.1.0")}),1.0]])]});
            var Q52;
            {var subQ0=sQuery(id+"F4.wireOp",EDGE,"E7");var subQ1=sQuery(id+"F4.wireOp",EDGE,"E6");var subQ2=makeQuery(id+"F4.imprint","INTERSECT",VERTEX,{"disambiguationData":[OD(0.0)],"derivedFrom":[subQ1,subQ0]});Q52=makeQuery(id+"F4.imprint","IMPRINT",FACE,{"disambiguationData":[TD([[makeQuery(id+"F4.imprint","IMPRINT",EDGE,{"disambiguationData":[TD([[subQ2,-1.0]])],"derivedFrom":subQ1}),-1.0]])]});}
            var Q53;
            {var subQ0=sQuery(id+"F4.wireOp",EDGE,"E7");var subQ1=sQuery(id+"F4.wireOp",EDGE,"E6");var subQ2=makeQuery(id+"F4.imprint","INTERSECT",VERTEX,{"disambiguationData":[OD(0.0)],"derivedFrom":[subQ1,subQ0]});Q53=makeQuery(id+"F4.imprint","IMPRINT",FACE,{"disambiguationData":[TD([[makeQuery(id+"F4.imprint","IMPRINT",EDGE,{"disambiguationData":[TD([[subQ2,-1.0]])],"derivedFrom":subQ1}),1.0]])]});}
            var Q54;
            Q54=sQuery(id+"F4.wireOp",EDGE,"E9.1.1.0");
            var Q55;
            Q55=sQuery(id+"F4.wireOp",EDGE,"E9.1.1.1");
            extrude(context, id + "F5", {"entities" : qUnion([Q0, Q1, Q2, Q3, Q4, Q5, Q6, Q7, Q8, Q9, Q10, Q11, Q12, Q13, Q14, Q15, Q16, Q17, Q18, Q19, Q20, Q21, Q22, Q23, Q24, Q25, Q26, Q27, Q28, Q29, Q30, Q31, Q32, Q33, Q34, Q35, Q36, Q37, Q38, Q39, Q40, Q41, Q42, Q43, Q44, Q45, Q46, Q47, Q48, Q49, Q50, Q51, Q52, Q53]), "operationType" : NewBodyOperationType.ADD, "surfaceEntities" : qUnion([Q54, Q55]), "depth" : 1.59 * mm});
        }
        {
            var Q0;
            {var subQ0=sQuery(id+"F4.wireOp",EDGE,"E9.5.5.0");var subQ1=sQuery(id+"F0.wireOp",EDGE,"E5");var subQ2=makeQuery(id+"F3.opShell","OFFSET_EDGE",EDGE,{"disambiguationData":[OSD([subQ1]),TDD([makeQuery(id+"F1.opExtrude","CAP_EDGE",EDGE,{"disambiguationData":[OSD([subQ1])],"isStart":false})])]});var subQ3=makeQuery(id+"F4.imprint","INTERSECT",VERTEX,{"disambiguationData":[OD(0.0)],"derivedFrom":[subQ2,subQ0]});Q0=makeQuery(id+"F4.imprint","IMPRINT",FACE,{"disambiguationData":[TD([[makeQuery(id+"F4.imprint","IMPRINT",EDGE,{"disambiguationData":[TD([[subQ3,-1.0]])],"derivedFrom":subQ0}),1.0]])]});}
            var Q1;
            {var subQ0=sQuery(id+"F4.wireOp",EDGE,"E9.5.5.0");var subQ1=sQuery(id+"F0.wireOp",EDGE,"E5");var subQ2=makeQuery(id+"F3.opShell","OFFSET_EDGE",EDGE,{"disambiguationData":[OSD([subQ1]),TDD([makeQuery(id+"F1.opExtrude","CAP_EDGE",EDGE,{"disambiguationData":[OSD([subQ1])],"isStart":false})])]});var subQ3=makeQuery(id+"F4.imprint","INTERSECT",VERTEX,{"disambiguationData":[OD(0.0)],"derivedFrom":[subQ2,subQ0]});Q1=makeQuery(id+"F4.imprint","IMPRINT",FACE,{"disambiguationData":[TD([[makeQuery(id+"F4.imprint","IMPRINT",EDGE,{"disambiguationData":[TD([[subQ3,1.0]])],"derivedFrom":subQ0}),1.0]])]});}
            var Q2;
            {var subQ0=sQuery(id+"F4.wireOp",EDGE,"E9.4.6.0");var subQ1=sQuery(id+"F0.wireOp",EDGE,"E5");var subQ2=makeQuery(id+"F3.opShell","OFFSET_EDGE",EDGE,{"disambiguationData":[OSD([subQ1]),TDD([makeQuery(id+"F1.opExtrude","CAP_EDGE",EDGE,{"disambiguationData":[OSD([subQ1])],"isStart":false})])]});var subQ3=makeQuery(id+"F4.imprint","INTERSECT",VERTEX,{"disambiguationData":[OD(0.0)],"derivedFrom":[subQ2,subQ0]});Q2=makeQuery(id+"F4.imprint","IMPRINT",FACE,{"disambiguationData":[TD([[makeQuery(id+"F4.imprint","IMPRINT",EDGE,{"disambiguationData":[TD([[subQ3,-1.0]])],"derivedFrom":subQ0}),1.0]])]});}
            var Q3;
            {var subQ0=sQuery(id+"F4.wireOp",EDGE,"E9.4.6.0");var subQ1=sQuery(id+"F0.wireOp",EDGE,"E5");var subQ2=makeQuery(id+"F3.opShell","OFFSET_EDGE",EDGE,{"disambiguationData":[OSD([subQ1]),TDD([makeQuery(id+"F1.opExtrude","CAP_EDGE",EDGE,{"disambiguationData":[OSD([subQ1])],"isStart":false})])]});var subQ3=makeQuery(id+"F4.imprint","INTERSECT",VERTEX,{"disambiguationData":[OD(0.0)],"derivedFrom":[subQ2,subQ0]});Q3=makeQuery(id+"F4.imprint","IMPRINT",FACE,{"disambiguationData":[TD([[makeQuery(id+"F4.imprint","IMPRINT",EDGE,{"disambiguationData":[TD([[subQ3,1.0]])],"derivedFrom":subQ0}),1.0]])]});}
            var Q4;
            {var subQ0=sQuery(id+"F4.wireOp",EDGE,"E9.3.7.0");var subQ1=sQuery(id+"F0.wireOp",EDGE,"E5");var subQ2=makeQuery(id+"F3.opShell","OFFSET_EDGE",EDGE,{"disambiguationData":[OSD([subQ1]),TDD([makeQuery(id+"F1.opExtrude","CAP_EDGE",EDGE,{"disambiguationData":[OSD([subQ1])],"isStart":false})])]});var subQ3=makeQuery(id+"F4.imprint","INTERSECT",VERTEX,{"disambiguationData":[OD(0.0)],"derivedFrom":[subQ2,subQ0]});Q4=makeQuery(id+"F4.imprint","IMPRINT",FACE,{"disambiguationData":[TD([[makeQuery(id+"F4.imprint","IMPRINT",EDGE,{"disambiguationData":[TD([[subQ3,-1.0]])],"derivedFrom":subQ0}),1.0]])]});}
            var Q5;
            {var subQ0=sQuery(id+"F4.wireOp",EDGE,"E9.3.7.0");var subQ1=sQuery(id+"F0.wireOp",EDGE,"E5");var subQ2=makeQuery(id+"F3.opShell","OFFSET_EDGE",EDGE,{"disambiguationData":[OSD([subQ1]),TDD([makeQuery(id+"F1.opExtrude","CAP_EDGE",EDGE,{"disambiguationData":[OSD([subQ1])],"isStart":false})])]});var subQ3=makeQuery(id+"F4.imprint","INTERSECT",VERTEX,{"disambiguationData":[OD(0.0)],"derivedFrom":[subQ2,subQ0]});Q5=makeQuery(id+"F4.imprint","IMPRINT",FACE,{"disambiguationData":[TD([[makeQuery(id+"F4.imprint","IMPRINT",EDGE,{"disambiguationData":[TD([[subQ3,1.0]])],"derivedFrom":subQ0}),1.0]])]});}
            var Q6;
            {var subQ0=sQuery(id+"F4.wireOp",EDGE,"E9.2.8.0");var subQ1=sQuery(id+"F0.wireOp",EDGE,"E5");var subQ2=makeQuery(id+"F3.opShell","OFFSET_EDGE",EDGE,{"disambiguationData":[OSD([subQ1]),TDD([makeQuery(id+"F1.opExtrude","CAP_EDGE",EDGE,{"disambiguationData":[OSD([subQ1])],"isStart":false})])]});var subQ3=makeQuery(id+"F4.imprint","INTERSECT",VERTEX,{"disambiguationData":[OD(0.0)],"derivedFrom":[subQ2,subQ0]});Q6=makeQuery(id+"F4.imprint","IMPRINT",FACE,{"disambiguationData":[TD([[makeQuery(id+"F4.imprint","IMPRINT",EDGE,{"disambiguationData":[TD([[subQ3,-1.0]])],"derivedFrom":subQ0}),1.0]])]});}
            var Q7;
            {var subQ0=sQuery(id+"F4.wireOp",EDGE,"E9.2.8.0");var subQ1=sQuery(id+"F0.wireOp",EDGE,"E5");var subQ2=makeQuery(id+"F3.opShell","OFFSET_EDGE",EDGE,{"disambiguationData":[OSD([subQ1]),TDD([makeQuery(id+"F1.opExtrude","CAP_EDGE",EDGE,{"disambiguationData":[OSD([subQ1])],"isStart":false})])]});var subQ3=makeQuery(id+"F4.imprint","INTERSECT",VERTEX,{"disambiguationData":[OD(0.0)],"derivedFrom":[subQ2,subQ0]});Q7=makeQuery(id+"F4.imprint","IMPRINT",FACE,{"disambiguationData":[TD([[makeQuery(id+"F4.imprint","IMPRINT",EDGE,{"disambiguationData":[TD([[subQ3,1.0]])],"derivedFrom":subQ0}),1.0]])]});}
            var Q8;
            {var subQ0=sQuery(id+"F4.wireOp",EDGE,"E9.6.4.0");var subQ1=sQuery(id+"F0.wireOp",EDGE,"E5");var subQ2=makeQuery(id+"F3.opShell","OFFSET_EDGE",EDGE,{"disambiguationData":[OSD([subQ1]),TDD([makeQuery(id+"F1.opExtrude","CAP_EDGE",EDGE,{"disambiguationData":[OSD([subQ1])],"isStart":false})])]});var subQ3=makeQuery(id+"F4.imprint","INTERSECT",VERTEX,{"disambiguationData":[OD(0.0)],"derivedFrom":[subQ2,subQ0]});Q8=makeQuery(id+"F4.imprint","IMPRINT",FACE,{"disambiguationData":[TD([[makeQuery(id+"F4.imprint","IMPRINT",EDGE,{"disambiguationData":[TD([[subQ3,1.0]])],"derivedFrom":subQ0}),1.0]])]});}
            var Q9;
            {var subQ0=sQuery(id+"F4.wireOp",EDGE,"E9.6.4.0");var subQ1=sQuery(id+"F0.wireOp",EDGE,"E5");var subQ2=makeQuery(id+"F3.opShell","OFFSET_EDGE",EDGE,{"disambiguationData":[OSD([subQ1]),TDD([makeQuery(id+"F1.opExtrude","CAP_EDGE",EDGE,{"disambiguationData":[OSD([subQ1])],"isStart":false})])]});var subQ3=makeQuery(id+"F4.imprint","INTERSECT",VERTEX,{"disambiguationData":[OD(0.0)],"derivedFrom":[subQ2,subQ0]});Q9=makeQuery(id+"F4.imprint","IMPRINT",FACE,{"disambiguationData":[TD([[makeQuery(id+"F4.imprint","IMPRINT",EDGE,{"disambiguationData":[TD([[subQ3,-1.0]])],"derivedFrom":subQ0}),1.0]])]});}
            var Q10;
            {var subQ0=sQuery(id+"F4.wireOp",EDGE,"E9.7.3.0");var subQ1=sQuery(id+"F0.wireOp",EDGE,"E5");var subQ2=makeQuery(id+"F3.opShell","OFFSET_EDGE",EDGE,{"disambiguationData":[OSD([subQ1]),TDD([makeQuery(id+"F1.opExtrude","CAP_EDGE",EDGE,{"disambiguationData":[OSD([subQ1])],"isStart":false})])]});var subQ3=makeQuery(id+"F4.imprint","INTERSECT",VERTEX,{"disambiguationData":[OD(0.0)],"derivedFrom":[subQ2,subQ0]});Q10=makeQuery(id+"F4.imprint","IMPRINT",FACE,{"disambiguationData":[TD([[makeQuery(id+"F4.imprint","IMPRINT",EDGE,{"disambiguationData":[TD([[subQ3,1.0]])],"derivedFrom":subQ0}),1.0]])]});}
            var Q11;
            {var subQ0=sQuery(id+"F4.wireOp",EDGE,"E9.7.3.0");var subQ1=sQuery(id+"F0.wireOp",EDGE,"E5");var subQ2=makeQuery(id+"F3.opShell","OFFSET_EDGE",EDGE,{"disambiguationData":[OSD([subQ1]),TDD([makeQuery(id+"F1.opExtrude","CAP_EDGE",EDGE,{"disambiguationData":[OSD([subQ1])],"isStart":false})])]});var subQ3=makeQuery(id+"F4.imprint","INTERSECT",VERTEX,{"disambiguationData":[OD(0.0)],"derivedFrom":[subQ2,subQ0]});Q11=makeQuery(id+"F4.imprint","IMPRINT",FACE,{"disambiguationData":[TD([[makeQuery(id+"F4.imprint","IMPRINT",EDGE,{"disambiguationData":[TD([[subQ3,-1.0]])],"derivedFrom":subQ0}),1.0]])]});}
            var Q12;
            {var subQ0=sQuery(id+"F4.wireOp",EDGE,"E9.8.2.0");var subQ1=sQuery(id+"F0.wireOp",EDGE,"E5");var subQ2=makeQuery(id+"F3.opShell","OFFSET_EDGE",EDGE,{"disambiguationData":[OSD([subQ1]),TDD([makeQuery(id+"F1.opExtrude","CAP_EDGE",EDGE,{"disambiguationData":[OSD([subQ1])],"isStart":false})])]});var subQ3=makeQuery(id+"F4.imprint","INTERSECT",VERTEX,{"disambiguationData":[OD(0.0)],"derivedFrom":[subQ2,subQ0]});Q12=makeQuery(id+"F4.imprint","IMPRINT",FACE,{"disambiguationData":[TD([[makeQuery(id+"F4.imprint","IMPRINT",EDGE,{"disambiguationData":[TD([[subQ3,1.0]])],"derivedFrom":subQ0}),1.0]])]});}
            var Q13;
            {var subQ0=sQuery(id+"F4.wireOp",EDGE,"E9.8.2.0");var subQ1=sQuery(id+"F0.wireOp",EDGE,"E5");var subQ2=makeQuery(id+"F3.opShell","OFFSET_EDGE",EDGE,{"disambiguationData":[OSD([subQ1]),TDD([makeQuery(id+"F1.opExtrude","CAP_EDGE",EDGE,{"disambiguationData":[OSD([subQ1])],"isStart":false})])]});var subQ3=makeQuery(id+"F4.imprint","INTERSECT",VERTEX,{"disambiguationData":[OD(0.0)],"derivedFrom":[subQ2,subQ0]});Q13=makeQuery(id+"F4.imprint","IMPRINT",FACE,{"disambiguationData":[TD([[makeQuery(id+"F4.imprint","IMPRINT",EDGE,{"disambiguationData":[TD([[subQ3,-1.0]])],"derivedFrom":subQ0}),1.0]])]});}
            var Q14;
            {var subQ0=sQuery(id+"F4.wireOp",EDGE,"E9.6.4.1");var subQ1=sQuery(id+"F0.wireOp",EDGE,"E5");var subQ2=makeQuery(id+"F3.opShell","OFFSET_EDGE",EDGE,{"disambiguationData":[OSD([subQ1]),TDD([makeQuery(id+"F1.opExtrude","CAP_EDGE",EDGE,{"disambiguationData":[OSD([subQ1])],"isStart":false})])]});var subQ3=makeQuery(id+"F4.imprint","INTERSECT",VERTEX,{"disambiguationData":[OD(0.0)],"derivedFrom":[subQ2,subQ0]});Q14=makeQuery(id+"F4.imprint","IMPRINT",FACE,{"disambiguationData":[TD([[makeQuery(id+"F4.imprint","IMPRINT",EDGE,{"disambiguationData":[TD([[subQ3,1.0]])],"derivedFrom":subQ0}),1.0]])]});}
            var Q15;
            {var subQ0=sQuery(id+"F4.wireOp",EDGE,"E9.7.3.1");var subQ1=sQuery(id+"F0.wireOp",EDGE,"E5");var subQ2=makeQuery(id+"F3.opShell","OFFSET_EDGE",EDGE,{"disambiguationData":[OSD([subQ1]),TDD([makeQuery(id+"F1.opExtrude","CAP_EDGE",EDGE,{"disambiguationData":[OSD([subQ1])],"isStart":false})])]});var subQ3=makeQuery(id+"F4.imprint","INTERSECT",VERTEX,{"disambiguationData":[OD(0.0)],"derivedFrom":[subQ2,subQ0]});Q15=makeQuery(id+"F4.imprint","IMPRINT",FACE,{"disambiguationData":[TD([[makeQuery(id+"F4.imprint","IMPRINT",EDGE,{"disambiguationData":[TD([[subQ3,1.0]])],"derivedFrom":subQ0}),1.0]])]});}
            var Q16;
            {var subQ0=sQuery(id+"F4.wireOp",EDGE,"E9.8.2.1");var subQ1=sQuery(id+"F0.wireOp",EDGE,"E5");var subQ2=makeQuery(id+"F3.opShell","OFFSET_EDGE",EDGE,{"disambiguationData":[OSD([subQ1]),TDD([makeQuery(id+"F1.opExtrude","CAP_EDGE",EDGE,{"disambiguationData":[OSD([subQ1])],"isStart":false})])]});var subQ3=makeQuery(id+"F4.imprint","INTERSECT",VERTEX,{"disambiguationData":[OD(0.0)],"derivedFrom":[subQ2,subQ0]});Q16=makeQuery(id+"F4.imprint","IMPRINT",FACE,{"disambiguationData":[TD([[makeQuery(id+"F4.imprint","IMPRINT",EDGE,{"disambiguationData":[TD([[subQ3,1.0]])],"derivedFrom":subQ0}),1.0]])]});}
            var Q17;
            {var subQ0=sQuery(id+"F4.wireOp",EDGE,"E9.6.4.1");var subQ1=sQuery(id+"F0.wireOp",EDGE,"E5");var subQ2=makeQuery(id+"F3.opShell","OFFSET_EDGE",EDGE,{"disambiguationData":[OSD([subQ1]),TDD([makeQuery(id+"F1.opExtrude","CAP_EDGE",EDGE,{"disambiguationData":[OSD([subQ1])],"isStart":false})])]});var subQ3=makeQuery(id+"F4.imprint","INTERSECT",VERTEX,{"disambiguationData":[OD(0.0)],"derivedFrom":[subQ2,subQ0]});Q17=makeQuery(id+"F4.imprint","IMPRINT",FACE,{"disambiguationData":[TD([[makeQuery(id+"F4.imprint","IMPRINT",EDGE,{"disambiguationData":[TD([[subQ3,-1.0]])],"derivedFrom":subQ0}),1.0]])]});}
            var Q18;
            {var subQ0=sQuery(id+"F4.wireOp",EDGE,"E9.7.3.1");var subQ1=sQuery(id+"F0.wireOp",EDGE,"E5");var subQ2=makeQuery(id+"F3.opShell","OFFSET_EDGE",EDGE,{"disambiguationData":[OSD([subQ1]),TDD([makeQuery(id+"F1.opExtrude","CAP_EDGE",EDGE,{"disambiguationData":[OSD([subQ1])],"isStart":false})])]});var subQ3=makeQuery(id+"F4.imprint","INTERSECT",VERTEX,{"disambiguationData":[OD(0.0)],"derivedFrom":[subQ2,subQ0]});Q18=makeQuery(id+"F4.imprint","IMPRINT",FACE,{"disambiguationData":[TD([[makeQuery(id+"F4.imprint","IMPRINT",EDGE,{"disambiguationData":[TD([[subQ3,-1.0]])],"derivedFrom":subQ0}),1.0]])]});}
            var Q19;
            {var subQ0=sQuery(id+"F4.wireOp",EDGE,"E9.8.2.1");var subQ1=sQuery(id+"F0.wireOp",EDGE,"E5");var subQ2=makeQuery(id+"F3.opShell","OFFSET_EDGE",EDGE,{"disambiguationData":[OSD([subQ1]),TDD([makeQuery(id+"F1.opExtrude","CAP_EDGE",EDGE,{"disambiguationData":[OSD([subQ1])],"isStart":false})])]});var subQ3=makeQuery(id+"F4.imprint","INTERSECT",VERTEX,{"disambiguationData":[OD(0.0)],"derivedFrom":[subQ2,subQ0]});Q19=makeQuery(id+"F4.imprint","IMPRINT",FACE,{"disambiguationData":[TD([[makeQuery(id+"F4.imprint","IMPRINT",EDGE,{"disambiguationData":[TD([[subQ3,-1.0]])],"derivedFrom":subQ0}),1.0]])]});}
            var Q20;
            {var subQ0=sQuery(id+"F4.wireOp",EDGE,"E9.5.5.1");var subQ1=sQuery(id+"F0.wireOp",EDGE,"E5");var subQ2=makeQuery(id+"F3.opShell","OFFSET_EDGE",EDGE,{"disambiguationData":[OSD([subQ1]),TDD([makeQuery(id+"F1.opExtrude","CAP_EDGE",EDGE,{"disambiguationData":[OSD([subQ1])],"isStart":false})])]});var subQ3=makeQuery(id+"F4.imprint","INTERSECT",VERTEX,{"disambiguationData":[OD(0.0)],"derivedFrom":[subQ2,subQ0]});Q20=makeQuery(id+"F4.imprint","IMPRINT",FACE,{"disambiguationData":[TD([[makeQuery(id+"F4.imprint","IMPRINT",EDGE,{"disambiguationData":[TD([[subQ3,-1.0]])],"derivedFrom":subQ0}),1.0]])]});}
            var Q21;
            {var subQ0=sQuery(id+"F4.wireOp",EDGE,"E9.5.5.1");var subQ1=sQuery(id+"F0.wireOp",EDGE,"E5");var subQ2=makeQuery(id+"F3.opShell","OFFSET_EDGE",EDGE,{"disambiguationData":[OSD([subQ1]),TDD([makeQuery(id+"F1.opExtrude","CAP_EDGE",EDGE,{"disambiguationData":[OSD([subQ1])],"isStart":false})])]});var subQ3=makeQuery(id+"F4.imprint","INTERSECT",VERTEX,{"disambiguationData":[OD(0.0)],"derivedFrom":[subQ2,subQ0]});Q21=makeQuery(id+"F4.imprint","IMPRINT",FACE,{"disambiguationData":[TD([[makeQuery(id+"F4.imprint","IMPRINT",EDGE,{"disambiguationData":[TD([[subQ3,1.0]])],"derivedFrom":subQ0}),1.0]])]});}
            var Q22;
            {var subQ0=sQuery(id+"F4.wireOp",EDGE,"E9.4.6.1");var subQ1=sQuery(id+"F0.wireOp",EDGE,"E5");var subQ2=makeQuery(id+"F3.opShell","OFFSET_EDGE",EDGE,{"disambiguationData":[OSD([subQ1]),TDD([makeQuery(id+"F1.opExtrude","CAP_EDGE",EDGE,{"disambiguationData":[OSD([subQ1])],"isStart":false})])]});var subQ3=makeQuery(id+"F4.imprint","INTERSECT",VERTEX,{"disambiguationData":[OD(0.0)],"derivedFrom":[subQ2,subQ0]});Q22=makeQuery(id+"F4.imprint","IMPRINT",FACE,{"disambiguationData":[TD([[makeQuery(id+"F4.imprint","IMPRINT",EDGE,{"disambiguationData":[TD([[subQ3,-1.0]])],"derivedFrom":subQ0}),1.0]])]});}
            var Q23;
            {var subQ0=sQuery(id+"F4.wireOp",EDGE,"E9.4.6.1");var subQ1=sQuery(id+"F0.wireOp",EDGE,"E5");var subQ2=makeQuery(id+"F3.opShell","OFFSET_EDGE",EDGE,{"disambiguationData":[OSD([subQ1]),TDD([makeQuery(id+"F1.opExtrude","CAP_EDGE",EDGE,{"disambiguationData":[OSD([subQ1])],"isStart":false})])]});var subQ3=makeQuery(id+"F4.imprint","INTERSECT",VERTEX,{"disambiguationData":[OD(0.0)],"derivedFrom":[subQ2,subQ0]});Q23=makeQuery(id+"F4.imprint","IMPRINT",FACE,{"disambiguationData":[TD([[makeQuery(id+"F4.imprint","IMPRINT",EDGE,{"disambiguationData":[TD([[subQ3,1.0]])],"derivedFrom":subQ0}),1.0]])]});}
            var Q24;
            {var subQ0=sQuery(id+"F4.wireOp",EDGE,"E9.3.7.1");var subQ1=sQuery(id+"F0.wireOp",EDGE,"E5");var subQ2=makeQuery(id+"F3.opShell","OFFSET_EDGE",EDGE,{"disambiguationData":[OSD([subQ1]),TDD([makeQuery(id+"F1.opExtrude","CAP_EDGE",EDGE,{"disambiguationData":[OSD([subQ1])],"isStart":false})])]});var subQ3=makeQuery(id+"F4.imprint","INTERSECT",VERTEX,{"disambiguationData":[OD(0.0)],"derivedFrom":[subQ2,subQ0]});Q24=makeQuery(id+"F4.imprint","IMPRINT",FACE,{"disambiguationData":[TD([[makeQuery(id+"F4.imprint","IMPRINT",EDGE,{"disambiguationData":[TD([[subQ3,-1.0]])],"derivedFrom":subQ0}),1.0]])]});}
            var Q25;
            {var subQ0=sQuery(id+"F4.wireOp",EDGE,"E9.3.7.1");var subQ1=sQuery(id+"F0.wireOp",EDGE,"E5");var subQ2=makeQuery(id+"F3.opShell","OFFSET_EDGE",EDGE,{"disambiguationData":[OSD([subQ1]),TDD([makeQuery(id+"F1.opExtrude","CAP_EDGE",EDGE,{"disambiguationData":[OSD([subQ1])],"isStart":false})])]});var subQ3=makeQuery(id+"F4.imprint","INTERSECT",VERTEX,{"disambiguationData":[OD(0.0)],"derivedFrom":[subQ2,subQ0]});Q25=makeQuery(id+"F4.imprint","IMPRINT",FACE,{"disambiguationData":[TD([[makeQuery(id+"F4.imprint","IMPRINT",EDGE,{"disambiguationData":[TD([[subQ3,1.0]])],"derivedFrom":subQ0}),1.0]])]});}
            var Q26;
            {var subQ0=sQuery(id+"F4.wireOp",EDGE,"E9.2.8.1");var subQ1=sQuery(id+"F0.wireOp",EDGE,"E5");var subQ2=makeQuery(id+"F3.opShell","OFFSET_EDGE",EDGE,{"disambiguationData":[OSD([subQ1]),TDD([makeQuery(id+"F1.opExtrude","CAP_EDGE",EDGE,{"disambiguationData":[OSD([subQ1])],"isStart":false})])]});var subQ3=makeQuery(id+"F4.imprint","INTERSECT",VERTEX,{"disambiguationData":[OD(0.0)],"derivedFrom":[subQ2,subQ0]});Q26=makeQuery(id+"F4.imprint","IMPRINT",FACE,{"disambiguationData":[TD([[makeQuery(id+"F4.imprint","IMPRINT",EDGE,{"disambiguationData":[TD([[subQ3,1.0]])],"derivedFrom":subQ0}),1.0]])]});}
            var Q27;
            {var subQ0=sQuery(id+"F4.wireOp",EDGE,"E9.2.8.1");var subQ1=sQuery(id+"F0.wireOp",EDGE,"E5");var subQ2=makeQuery(id+"F3.opShell","OFFSET_EDGE",EDGE,{"disambiguationData":[OSD([subQ1]),TDD([makeQuery(id+"F1.opExtrude","CAP_EDGE",EDGE,{"disambiguationData":[OSD([subQ1])],"isStart":false})])]});var subQ3=makeQuery(id+"F4.imprint","INTERSECT",VERTEX,{"disambiguationData":[OD(0.0)],"derivedFrom":[subQ2,subQ0]});Q27=makeQuery(id+"F4.imprint","IMPRINT",FACE,{"disambiguationData":[TD([[makeQuery(id+"F4.imprint","IMPRINT",EDGE,{"disambiguationData":[TD([[subQ3,-1.0]])],"derivedFrom":subQ0}),1.0]])]});}
            extrude(context, id + "F6", {"entities" : qUnion([Q0, Q1, Q2, Q3, Q4, Q5, Q6, Q7, Q8, Q9, Q10, Q11, Q12, Q13, Q14, Q15, Q16, Q17, Q18, Q19, Q20, Q21, Q22, Q23, Q24, Q25, Q26, Q27]), "operationType" : NewBodyOperationType.REMOVE, "depth" : 25.4 * mm});
        }
    });
